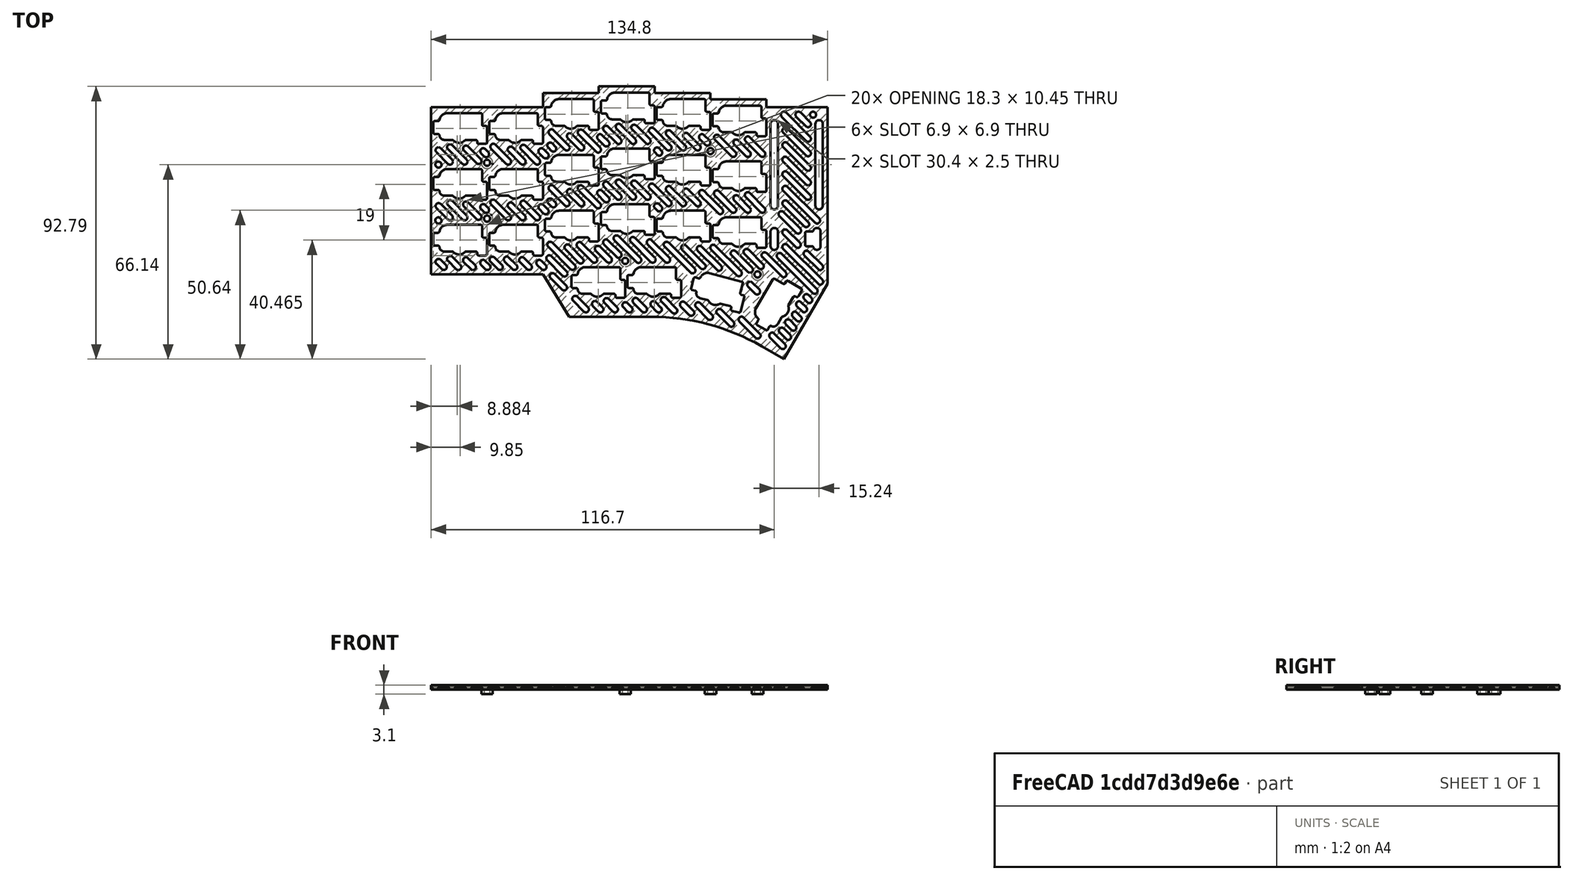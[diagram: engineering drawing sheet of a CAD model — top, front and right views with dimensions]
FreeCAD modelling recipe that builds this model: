
FCSTD DOCUMENT  (FreeCAD 0.22R37213 (Git))
Label: key-v3
License: All rights reserved
LicenseURL: https://en.wikipedia.org/wiki/All_rights_reserved
objects: Sketcher::SketchObject×8, PartDesign::Pocket×5, PartDesign::Pad×4, Part::Part2DObjectPython×3, PartDesign::Body×3, Part::Cut×3, App::Link×2, PartDesign::LinearPattern×2, Spreadsheet::Sheet×1, Part::FeaturePython×1, PartDesign::FeatureBase×1, PartDesign::Plane×1
note: 40 computed .brp shape members not serialized (recipe doc carries the construction recipe); baked Part::Feature solids carry a one-line shape summary decoded from their .brp

FEATURE [Sketcher::SketchObject] Sketch  label="smd cutout"
  FullyConstrained = true
  sketch-geometry (67):
    g0: LineSegment StartX=-9.5 StartY=-9.5 StartZ=0 EndX=9.5 EndY=-9.5 EndZ=0
    g1: LineSegment StartX=9.5 StartY=-9.5 StartZ=0 EndX=9.5 EndY=9.5 EndZ=0
    g2: LineSegment StartX=9.5 StartY=9.5 StartZ=0 EndX=-9.5 EndY=9.5 EndZ=0
    g3: LineSegment StartX=-9.5 StartY=9.5 StartZ=0 EndX=-9.5 EndY=-9.5 EndZ=0
    g4: Circle CenterX=-3.81 CenterY=2.54 CenterZ=0 NormalX=0 NormalY=0 NormalZ=1 AngleXU=0 Radius=1.5
    g5: Circle CenterX=2.54 CenterY=5.08 CenterZ=0 NormalX=0 NormalY=0 NormalZ=1 AngleXU=0 Radius=1.5
    g6: Circle CenterX=0 CenterY=0 CenterZ=0 NormalX=0 NormalY=0 NormalZ=1 AngleXU=0 Radius=2
    g7: Circle CenterX=5 CenterY=0 CenterZ=0 NormalX=0 NormalY=0 NormalZ=1 AngleXU=0 Radius=1
    g8: Circle CenterX=-5 CenterY=0 CenterZ=0 NormalX=0 NormalY=0 NormalZ=1 AngleXU=0 Radius=1
    g9: GeomPoint X=-8.5 Y=1 Z=0
    g10: GeomPoint X=-8.5 Y=4 Z=0
    g11: GeomPoint X=-6 Y=4 Z=0
    g12: GeomPoint X=-2.5 Y=1 Z=0
    g13: GeomPoint X=-0.4 Y=2.9 Z=0
    g14: GeomPoint X=4.5 Y=2.9 Z=0
    g15: GeomPoint X=4.5 Y=3.6 Z=0
    g16: GeomPoint X=7.1 Y=6.7 Z=0
    g17: GeomPoint X=-4 Y=6.7 Z=0
    g18: LineSegment StartX=-8.5 StartY=1 StartZ=0 EndX=-2.5 EndY=1 EndZ=0
    g19: LineSegment StartX=-8.5 StartY=1 StartZ=0 EndX=-8.5 EndY=4 EndZ=0
    g20: LineSegment StartX=-8.5 StartY=4 StartZ=0 EndX=-6 EndY=4 EndZ=0
    g21: LineSegment StartX=-6 StartY=4 StartZ=0 EndX=-6 EndY=4.7 EndZ=0
    g22: LineSegment StartX=-4 StartY=6.7 StartZ=0 EndX=7.1 EndY=6.7 EndZ=0
    g23: LineSegment StartX=7.1 StartY=6.7 StartZ=0 EndX=7.1 EndY=3.6 EndZ=0
    g24: LineSegment StartX=7.1 StartY=3.6 StartZ=0 EndX=4.5 EndY=3.6 EndZ=0
    g25: LineSegment StartX=4.5 StartY=2.9 StartZ=0 EndX=4.5 EndY=3.6 EndZ=0
    g26: LineSegment StartX=4.5 StartY=2.9 StartZ=0 EndX=-0.4 EndY=2.9 EndZ=0
    g27: ArcOfCircle CenterX=-0.4 CenterY=0.789474 CenterZ=0 NormalX=0 NormalY=0 NormalZ=1 AngleXU=0 Radius=2.11053 StartAngle=1.5708 EndAngle=3.04168
    g28: LineSegment StartX=6.85 StartY=2.35 StartZ=0 EndX=6.85 EndY=-2.35 EndZ=0
    g29: LineSegment StartX=6.85 StartY=-2.35 StartZ=0 EndX=9.15 EndY=-2.35 EndZ=0
    g30: LineSegment StartX=9.15 StartY=-2.35 StartZ=0 EndX=9.15 EndY=2.35 EndZ=0
    g31: ArcOfCircle CenterX=-4 CenterY=4.7 CenterZ=0 NormalX=0 NormalY=0 NormalZ=1 AngleXU=0 Radius=2 StartAngle=1.5708 EndAngle=3.14159
    g32: LineSegment StartX=6.85 StartY=2.35 StartZ=0 EndX=9.15 EndY=2.35 EndZ=0
    g33: LineSegment StartX=-8.8 StartY=0.8 StartZ=0 EndX=-8.8 EndY=4.2 EndZ=0
    g34: LineSegment StartX=-8.3 StartY=4.7 StartZ=0 EndX=-7.1607 EndY=4.7 EndZ=0
    g35: LineSegment StartX=-4 StartY=7.4 StartZ=0 EndX=7.3 EndY=7.4 EndZ=0
    g36: LineSegment StartX=7.8 StartY=6.9 StartZ=0 EndX=7.8 EndY=3.55 EndZ=0
    g37: LineSegment StartX=9.5 StartY=2.55 StartZ=0 EndX=9.5 EndY=-2.55 EndZ=0
    g38: LineSegment StartX=9 StartY=-3.05 StartZ=0 EndX=6.65 EndY=-3.05 EndZ=0
    g39: LineSegment StartX=-8.3 StartY=0.3 StartZ=0 EndX=-7.19089 EndY=0.3 EndZ=0
    g40: ArcOfCircle CenterX=-5 CenterY=0 CenterZ=0 NormalX=0 NormalY=0 NormalZ=1 AngleXU=0 Radius=1.7 StartAngle=3.23263 EndAngle=4.71239
    g41: ArcOfCircle CenterX=0 CenterY=0 CenterZ=0 NormalX=0 NormalY=0 NormalZ=1 AngleXU=0 Radius=2.7 StartAngle=3.89963 EndAngle=5.52514
    g42: LineSegment StartX=-5 StartY=-1.7 StartZ=0 EndX=-2.32379 EndY=-1.7 EndZ=0
    g43: LineSegment StartX=6.15 StartY=-2.55 StartZ=0 EndX=6.15 EndY=-2.2 EndZ=0
    g44: LineSegment StartX=2.32379 StartY=-1.7 StartZ=0 EndX=5.65 EndY=-1.7 EndZ=0
    g45: ArcOfCircle CenterX=-4 CenterY=4.7 CenterZ=0 NormalX=0 NormalY=0 NormalZ=1 AngleXU=0 Radius=2.7 StartAngle=1.5708 EndAngle=2.9847
    g46: ArcOfCircle CenterX=-2.32379 CenterY=-2.2 CenterZ=0 NormalX=0 NormalY=0 NormalZ=1 AngleXU=0 Radius=0.5 StartAngle=0.758041 EndAngle=1.5708
    g47: ArcOfCircle CenterX=2.32379 CenterY=-2.2 CenterZ=0 NormalX=0 NormalY=0 NormalZ=1 AngleXU=0 Radius=0.5 StartAngle=1.5708 EndAngle=2.38355
    g48: ArcOfCircle CenterX=5.65 CenterY=-2.2 CenterZ=0 NormalX=0 NormalY=0 NormalZ=1 AngleXU=0 Radius=0.5 StartAngle=0 EndAngle=1.5708
    g49: GeomPoint X=6.15 Y=-1.7 Z=0
    g50: ArcOfCircle CenterX=6.65 CenterY=-2.55 CenterZ=0 NormalX=0 NormalY=0 NormalZ=1 AngleXU=0 Radius=0.5 StartAngle=3.14159 EndAngle=4.71239
    g51: GeomPoint X=6.15 Y=-3.05 Z=0
    g52: ArcOfCircle CenterX=9 CenterY=-2.55 CenterZ=0 NormalX=0 NormalY=0 NormalZ=1 AngleXU=0 Radius=0.5 StartAngle=4.71239 EndAngle=6.28319
    g53: GeomPoint X=9.5 Y=-3.05 Z=0
    g54: LineSegment StartX=8.3 StartY=3.05 StartZ=0 EndX=9 EndY=3.05 EndZ=0
    g55: ArcOfCircle CenterX=9 CenterY=2.55 CenterZ=0 NormalX=0 NormalY=0 NormalZ=1 AngleXU=0 Radius=0.5 StartAngle=3e-16 EndAngle=1.5708
    g56: GeomPoint X=9.5 Y=3.05 Z=0
    g57: ArcOfCircle CenterX=8.3 CenterY=3.55 CenterZ=0 NormalX=0 NormalY=0 NormalZ=1 AngleXU=0 Radius=0.5 StartAngle=3.14159 EndAngle=4.71239
    g58: GeomPoint X=7.8 Y=3.05 Z=0
    g59: ArcOfCircle CenterX=7.3 CenterY=6.9 CenterZ=0 NormalX=0 NormalY=0 NormalZ=1 AngleXU=0 Radius=0.5 StartAngle=-9e-16 EndAngle=1.5708
    g60: GeomPoint X=7.8 Y=7.4 Z=0
    g61: ArcOfCircle CenterX=-7.1607 CenterY=5.2 CenterZ=0 NormalX=0 NormalY=0 NormalZ=1 AngleXU=0 Radius=0.5 StartAngle=4.71239 EndAngle=6.12629
    g62: ArcOfCircle CenterX=-8.3 CenterY=4.2 CenterZ=0 NormalX=0 NormalY=0 NormalZ=1 AngleXU=0 Radius=0.5 StartAngle=1.5708 EndAngle=3.14159
    g63: GeomPoint X=-8.8 Y=4.7 Z=0
    g64: ArcOfCircle CenterX=-8.3 CenterY=0.8 CenterZ=0 NormalX=0 NormalY=0 NormalZ=1 AngleXU=0 Radius=0.5 StartAngle=3.14159 EndAngle=4.71239
    g65: GeomPoint X=-8.8 Y=0.3 Z=0
    g66: ArcOfCircle CenterX=-7.19089 CenterY=-0.2 CenterZ=0 NormalX=0 NormalY=0 NormalZ=1 AngleXU=0 Radius=0.5 StartAngle=0.0910348 EndAngle=1.5708
  constraints (157):
    c: Coincident(g2,g3)
    c: Horizontal(g0)
    c: Horizontal(g2)
    c: Vertical(g1)
    c: PointOnObject(g7,g-1)
    c: Equal(g4,g5)
    c: Symmetric(g7,g8,g-2)
    c: Equal(g8,g7)
    c: DistanceX(g-1,g5) = 2.54
    c: Distance(g5,g-1) = 5.08
    c: DistanceX(g2,g2) = 19
    c: Equal(g2,g3)
    c: Distance(g4,g-2) = 3.81
    c: Distance(g4,g-1) = 2.54
    c: Distance(g8,g-2) = 5
    c: Distance(g9,g-1) = 1
    c: Coincident(g18,g9)
    c: Coincident(g18,g12)
    c: Horizontal(g18)
    c: Distance(g9,g-2) = 8.5
    c: Coincident(g19,g9)
    c: Coincident(g19,g10)
    c: Vertical(g19)
    c: Distance(g10,g-1) = 4
    c: Coincident(g20,g10)
    c: Coincident(g20,g11)
    c: Horizontal(g20)
    c: Distance(g11,g-2) = 6
    c: Distance(g17,g-2) = 4
    c: DistanceY(g-1,g17) = 6.7
    c: Coincident(g21,g11)
    c: Vertical(g21)
    c: Coincident(g22,g17)
    c: Coincident(g22,g16)
    c: Horizontal(g22)
    c: DistanceX(g-1,g16) = 7.1
    c: Coincident(g23,g16)
    c: Vertical(g23)
    c: Distance(g23,g-1) = 3.6
    c: Coincident(g24,g23)
    c: Coincident(g24,g15)
    c: Coincident(g25,g14)
    c: Coincident(g25,g15)
    c: Coincident(g26,g14)
    c: Coincident(g26,g13)
    c: Horizontal(g24)
    c: Horizontal(g26)
    c: Vertical(g25)
    c: Distance(g-2,g25) = 4.5
    c: Distance(g14,g-1) = 2.9
    c: Distance(g13,g-2) = 0.4
    c: Distance(g12,g-2) = 2.5
    c: Coincident(g27,g13)
    c: Coincident(g27,g12)
    c: Diameter(g5) = 3
    c: Diameter(g8) = 2
    c: Diameter(g6) = 4
    c: Vertical(g30)
    c: Horizontal(g29)
    c: Distance(g28,g-2) = 6.85
    c: Distance(g28,g-1) = 2.35
    c: Symmetric(g28,g28,g-1)
    c: Vertical(g3)
    c: Coincident(g31,g17)
    c: Tangent(g31,g21) = 1.5708
    c: Coincident(g32,g28)
    c: Coincident(g32,g30)
    c: Horizontal(g32)
    c: Coincident(g6,g-1)
    c: Symmetric(g0,g1,g6)
    c: Coincident(g3,g0)
    c: Coincident(g2,g1)
    c: Coincident(g1,g0)
    c: DistanceX(g29,g29) = 2.3
    c: Coincident(g29,g30)
    c: Coincident(g29,g28)
    c: Tangent(g27,g26)
    c: Tangent(g31,g22)
    c: Vertical(g33)
    c: Horizontal(g34)
    c: Horizontal(g35)
    c: Vertical(g36)
    c: PointOnObject(g56,g1)
    c: PointOnObject(g53,g1)
    c: Horizontal(g38)
    c: Horizontal(g39)
    c: Distance(g20,g34) = 0.7
    c: Distance(g65,g19) = 0.3
    c: Distance(g18,g39) = 0.7
    c: Coincident(g40,g8)
    c: Coincident(g41,g6)
    c: Horizontal(g42)
    c: Vertical(g43)
    c: Tangent(g44,g42)
    c: Distance(g28,g43) = 0.7
    c: Distance(g53,g29) = 0.7
    c: Tangent(g42,g40) = -1.5708
    c: Distance(g23,g36) = 0.7
    c: Distance(g35,g22) = 0.7
    c: Coincident(g45,g31)
    c: Tangent(g45,g35) = 1.5708
    c: Tangent(g42,g46) = 1.5708
    c: Tangent(g41,g46) = 1.5708
    c: Tangent(g41,g47) = 1.5708
    c: Tangent(g44,g47) = 1.5708
    c: PointOnObject(g49,g44)
    c: PointOnObject(g49,g43)
    c: Tangent(g44,g48) = 1.5708
    c: Tangent(g43,g48) = -1.5708
    c: PointOnObject(g51,g43)
    c: PointOnObject(g51,g38)
    c: Tangent(g43,g50) = 1.5708
    c: Tangent(g38,g50) = 1.5708
    c: PointOnObject(g53,g38)
    c: PointOnObject(g53,g37)
    c: Tangent(g38,g52) = 1.5708
    c: Tangent(g37,g52) = 1.5708
    c: Horizontal(g54)
    c: Distance(g32,g54) = 0.7
    c: PointOnObject(g56,g37)
    c: PointOnObject(g56,g54)
    c: Tangent(g37,g55) = 1.5708
    c: Tangent(g54,g55) = 1.5708
    c: PointOnObject(g58,g54)
    c: PointOnObject(g58,g36)
    c: Tangent(g54,g57) = -1.5708
    c: Tangent(g36,g57) = -1.5708
    c: PointOnObject(g60,g35)
    c: PointOnObject(g60,g36)
    c: Tangent(g35,g59) = 1.5708
    c: Tangent(g36,g59) = 1.5708
    c: Tangent(g34,g61) = -1.5708
    c: Tangent(g45,g61) = 1.5708
    c: PointOnObject(g63,g34)
    c: PointOnObject(g63,g33)
    c: Tangent(g34,g62) = 1.5708
    c: Tangent(g33,g62) = 1.5708
    c: PointOnObject(g65,g39)
    c: PointOnObject(g65,g33)
    c: Tangent(g39,g64) = -1.5708
    c: Tangent(g33,g64) = 1.5708
    c: Tangent(g40,g66) = 1.5708
    c: Tangent(g39,g66) = 1.5708
    c: Radius(g46) = 0.5
    c: Equal(g66,g64)
    c: Equal(g64,g46)
    c: Equal(g46,g47)
    c: Equal(g47,g48)
    c: Equal(g48,g50)
    c: Equal(g50,g57)
    c: Equal(g57,g59)
    c: Equal(g59,g61)
    c: Equal(g61,g62)
    c: Equal(g57,g55)
    c: Equal(g52,g50)
    c: Distance(g40,g8) = 0.7
    c: Distance(g41,g6) = 0.7
FEATURE [Spreadsheet::Sheet] Spreadsheet  label="constants"
  cells = A1(slot_height)=0.6; B1='slot height; A2(base_normal)=1.5; B2='base normal; A3(base_thin)=0.3; B3='base thin ; A4(fillet_small)=0.15; B4='fillet rounding
FEATURE [Part::Part2DObjectPython] Wire  # Draft 2D object (typed FeaturePython)
  Area = 0
  ChamferSize = 0
  Closed = false
  End = (95,2.6,0)
  FilletRadius = 0
  Length = 95.9778
  MakeFace = true
  Points = (6) [(0,0,0),(19,0,0),(38,4.8,0),(57,7,0),(76,4.8,0),(95,2.6,0)]
  Start = (0,0,0)
  Subdivisions = 0
FEATURE [Part::Part2DObjectPython] Wire001  label="main matrix wire"  # Draft 2D object (typed FeaturePython)
  Area = 0
  ChamferSize = 0
  Closed = false
  End = (95,2.6,0)
  FilletRadius = 0
  Length = 323.978
  MakeFace = false
  Points = (18) [(0,0,0),(0,-19,0),(0,-38,0),(19,-38,0),(19,-19,0),(19,0,0),(38,4.8,0),(38,-14.2,0),(38,-33.2,0),(57,-31,0),(57,-12,0),(57,7,0),(76,4.8,0),+5 more]
  Start = (0,0,0)
  Subdivisions = 0
FEATURE [Part::Part2DObjectPython] Wire002  label="horizonal matrix"  # Draft 2D object (typed FeaturePython)
  Area = 0
  ChamferSize = 0
  Closed = false
  End = (95,2.6,0)
  FilletRadius = 0
  Length = 368.271
  MakeFace = true
  Points = (20) [(0,0,0),(0,-19,0),(0,-38,0),(19,-38,0),(19,-19,0),(19,0,0),(38,4.8,0),(38,-14.2,0),(38,-33.2,0),(47,-52.4,0),(66,-52.4,0),(57,-31,0),(57,-12,0),+7 more]
  Start = (0,0,0)
  Subdivisions = 0
FEATURE [Sketcher::SketchObject] Sketch001  label="pcb contour"
  AttachmentSupport = -> [XY_Plane]
  FullyConstrained = true
  MapMode = 5
  expr: Constraints[36] = 19 * 3
  sketch-geometry (39):
    g0: LineSegment StartX=-9.5 StartY=9.5 StartZ=0 EndX=28.5 EndY=9.5 EndZ=0
    g1: LineSegment StartX=28.5 StartY=9.5 StartZ=0 EndX=28.5 EndY=14.3 EndZ=0
    g2: LineSegment StartX=28.5 StartY=14.3 StartZ=0 EndX=47.5 EndY=14.3 EndZ=0
    g3: LineSegment StartX=47.5 StartY=14.3 StartZ=0 EndX=47.5 EndY=16.5 EndZ=0
    g4: LineSegment StartX=47.5 StartY=16.5 StartZ=0 EndX=66.5 EndY=16.5 EndZ=0
    g5: LineSegment StartX=66.5 StartY=16.5 StartZ=0 EndX=66.5 EndY=14.3 EndZ=0
    g6: LineSegment StartX=66.5 StartY=14.3 StartZ=0 EndX=85.5 EndY=14.3 EndZ=0
    g7: LineSegment StartX=85.5 StartY=14.3 StartZ=0 EndX=85.5 EndY=12.1 EndZ=0
    g8: LineSegment StartX=85.5 StartY=12.1 StartZ=0 EndX=104.5 EndY=12.1 EndZ=0
    g9: LineSegment StartX=104.5 StartY=12.1 StartZ=0 EndX=104.5 EndY=9.4 EndZ=0
    g10: LineSegment StartX=104.5 StartY=9.4 StartZ=0 EndX=125.3 EndY=9.4 EndZ=0
    g11: LineSegment StartX=-9.5 StartY=9.5 StartZ=0 EndX=-9.5 EndY=-47.5 EndZ=0
    g12: LineSegment StartX=-9.5 StartY=-47.5 StartZ=0 EndX=28.5 EndY=-47.5 EndZ=0
    g13: LineSegment StartX=28.5 StartY=-47.5 StartZ=0 EndX=37.45 EndY=-61.9 EndZ=0
    g14: LineSegment StartX=37.45 StartY=-61.9 StartZ=0 EndX=56.45 EndY=-61.9 EndZ=0
    g15: LineSegment StartX=56.45 StartY=-61.9 StartZ=0 EndX=56.45 EndY=-42.9 EndZ=0
    g16: LineSegment StartX=56.45 StartY=-42.9 StartZ=0 EndX=37.45 EndY=-42.9 EndZ=0
    g17: LineSegment StartX=37.45 StartY=-42.9 StartZ=0 EndX=37.45 EndY=-61.9 EndZ=0
    g18: LineSegment StartX=56.45 StartY=-61.9 StartZ=0 EndX=75.45 EndY=-61.9 EndZ=0
    g19: LineSegment StartX=75.45 StartY=-61.9 StartZ=0 EndX=75.45 EndY=-42.9 EndZ=0
    g20: LineSegment StartX=75.45 StartY=-42.9 StartZ=0 EndX=56.45 EndY=-42.9 EndZ=0
    g21: LineSegment StartX=56.45 StartY=-42.9 StartZ=0 EndX=56.45 EndY=-61.9 EndZ=0
    g22: GeomPoint X=65.95 Y=-52.4 Z=0
    g23: LineSegment StartX=110.452 StartY=-76.2909 StartZ=0 EndX=93.9978 EndY=-66.7909 EndZ=0
    g24: LineSegment StartX=93.9978 StartY=-66.7909 StartZ=0 EndX=108.248 EndY=-42.1091 EndZ=0
    g25: LineSegment StartX=108.248 StartY=-42.1091 StartZ=0 EndX=124.702 EndY=-51.6091 EndZ=0
    g26: LineSegment StartX=124.702 StartY=-51.6091 StartZ=0 EndX=110.452 EndY=-76.2909 EndZ=0
    g27: GeomPoint X=109.35 Y=-59.2 Z=0
    g28: LineSegment StartX=75.5149 StartY=-61.9175 StartZ=0 EndX=80.4325 EndY=-43.5649 EndZ=0
    g29: LineSegment StartX=80.4325 StartY=-43.5649 StartZ=0 EndX=98.7851 EndY=-48.4825 EndZ=0
    g30: LineSegment StartX=98.7851 StartY=-48.4825 StartZ=0 EndX=93.8675 EndY=-66.8351 EndZ=0
    g31: LineSegment StartX=93.8675 StartY=-66.8351 StartZ=0 EndX=75.5149 EndY=-61.9175 EndZ=0
    g32: GeomPoint X=87.15 Y=-55.2 Z=0
    g33: LineSegment StartX=37.45 StartY=-61.9 StartZ=0 EndX=65.4303 EndY=-61.9 EndZ=0
    g34: LineSegment StartX=110.452 StartY=-76.2909 StartZ=0 EndX=102.93 EndY=-71.9481 EndZ=0
    g35: LineSegment StartX=125.3 StartY=9.4 StartZ=0 EndX=125.3 EndY=-50.5738 EndZ=0
    g36: LineSegment StartX=110.452 StartY=-76.2909 StartZ=0 EndX=125.3 EndY=-50.5738 EndZ=0
    g37: ArcOfCircle CenterX=65.4303 CenterY=-136.9 CenterZ=0 NormalX=0 NormalY=0 NormalZ=1 AngleXU=0 Radius=75 StartAngle=1.0472 EndAngle=1.5708
    g38: GeomPoint X=85.5265 Y=-61.9 Z=0
  constraints (105):
    c: Horizontal(g0)
    c: Coincident(g1,g0)
    c: Vertical(g1)
    c: Coincident(g2,g1)
    c: Horizontal(g2)
    c: Coincident(g3,g2)
    c: Vertical(g3)
    c: Coincident(g4,g3)
    c: Horizontal(g4)
    c: Coincident(g5,g4)
    c: Vertical(g5)
    c: Coincident(g6,g5)
    c: Horizontal(g6)
    c: Coincident(g7,g6)
    c: Vertical(g7)
    c: Coincident(g8,g7)
    c: Horizontal(g8)
    c: Coincident(g9,g8)
    c: Vertical(g9)
    c: Coincident(g10,g9)
    c: Horizontal(g10)
    c: DistanceX(g0,g-1) = 9.5
    c: Distance(g-1,g0) = 9.5
    c: DistanceX(g0,g0) = 38
    c: DistanceX(g2,g2) = 19
    c: Equal(g4,g2)
    c: Equal(g2,g6)
    c: Equal(g6,g8)
    c: DistanceY(g1,g1) = 4.8
    c: DistanceY(g3,g3) = 2.2
    c: DistanceY(g5,g5) = 2.2
    c: DistanceY(g7,g7) = 2.2
    c: DistanceY(g9,g9) = 2.7
    c: DistanceX(g10,g10) = 20.8
    c: Coincident(g11,g0)
    c: Vertical(g11)
    c: DistanceY(g11,g11) = 57
    c: Coincident(g12,g11)
    c: Horizontal(g12)
    c: DistanceX(g12,g12) = 38
    c: Coincident(g13,g12)
    c: DistanceX(g12,g13) = 8.95
    c: DistanceY(g13,g12) = 14.4
    c: Coincident(g14,g15)
    c: Coincident(g15,g16)
    c: Coincident(g16,g17)
    c: Coincident(g17,g14)
    c: Horizontal(g14)
    c: Horizontal(g16)
    c: Vertical(g15)
    c: Vertical(g17)
    c: Coincident(g14,g13)
    c: Equal(g17,g16)
    c: DistanceX(g16,g16) = 19
    c: Coincident(g18,g19)
    c: Coincident(g19,g20)
    c: Coincident(g20,g21)
    c: Coincident(g21,g18)
    c: Horizontal(g18)
    c: Horizontal(g20)
    c: Vertical(g19)
    c: Vertical(g21)
    c: Coincident(g18,g14)
    c: Equal(g20,g19)
    c: Equal(g19,g16)
    c: Symmetric(g14,g19,g22)
    c: Coincident(g24,g23)
    c: Coincident(g25,g24)
    c: Coincident(g26,g25)
    c: Coincident(g26,g23)
    c: Parallel(g25,g23)
    c: Parallel(g24,g26)
    c: Perpendicular(g25,g24)
    c: Equal(g23,g19)
    c: Symmetric(g25,g23,g27)
    c: Coincident(g29,g28)
    c: Coincident(g30,g29)
    c: Coincident(g31,g30)
    c: Coincident(g31,g28)
    c: Parallel(g30,g28)
    c: Parallel(g29,g31)
    c: Perpendicular(g30,g29)
    c: Equal(g29,g28)
    c: Symmetric(g30,g28,g32)
    c: Angle(g31,g18) = 0.261799
    c: Angle(g18,g26) = 1.0472
    c: DistanceX(g22,g32) = 21.2
    c: DistanceY(g32,g22) = 2.8
    c: Equal(g28,g19)
    c: DistanceX(g32,g27) = 22.2
    c: DistanceY(g27,g32) = 4
    c: Distance(g26,g26) = 28.5
    c: Coincident(g33,g13)
    c: Horizontal(g33)
    c: Tangent(g34,g23) = -1.5708
    c: Coincident(g35,g10)
    c: Vertical(g35)
    c: Coincident(g36,g23)
    c: Tangent(g26,g36)
    c: Coincident(g36,g35)
    c: PointOnObject(g38,g34)
    c: PointOnObject(g38,g33)
    c: Tangent(g34,g37) = -1.5708
    c: Tangent(g33,g37) = 1.5708
    c: Radius(g37) = 75
FEATURE [PartDesign::Pad] Pad  label="base"
  Direction = (0,0,1)
  Length = 1.5
  Length2 = 10
  Profile = -> Sketch001
  ReferenceAxis = -> Sketch001 [N_Axis]
  Suppressed = false
  Type = 0
  expr: Length = <<constants>>.base_normal
FEATURE [PartDesign::Body] Body  label="base body"
  Group = -> [Sketch001,Pad]
  Origin = -> Origin
  Tip = -> Pad
FEATURE [PartDesign::Pad] Pad001
  Direction = (0,0,1)
  Length = 1.5
  Length2 = 10
  Profile = -> Sketch
  ReferenceAxis = -> Sketch [N_Axis]
  Suppressed = false
  Type = 0
  expr: Length = <<constants>>.base_normal
FEATURE [PartDesign::Body] Body001  label="cutout"
  Group = -> [Sketch,Pad001]
  Origin = -> Origin001
  Tip = -> Pad001
FEATURE [Part::FeaturePython] PointArray  label="cutout array"  # Draft array (typed FeaturePython)
  Base = -> Body001
  Count = 20
  Fuse = false
  PointObject = -> Wire002
FEATURE [App::Link] Link  label="cutout001"
  LinkPlacement = pos=(87.2,-55.2,0) rot=(0,0,1;6.02139rad)
  LinkedObject = -> Body001
  Placement = pos=(87.2,-55.2,0) rot=(0,0,1;6.02139rad)
FEATURE [App::Link] Link001  label="cutout002"
  LinkPlacement = pos=(109.4,-59.2,0) rot=(0,0,1;1.0472rad)
  LinkedObject = -> Body001
  Placement = pos=(109.4,-59.2,0) rot=(0,0,1;1.0472rad)
FEATURE [Part::Cut] Cut
  Base = -> Body
  Tool = -> PointArray
FEATURE [Part::Cut] Cut001
  Base = -> Cut
  Tool = -> Link
FEATURE [Part::Cut] Cut002
  Base = -> Cut001
  Tool = -> Link001
FEATURE [PartDesign::FeatureBase] BaseFeature
  BaseFeature = -> Cut002
  Suppressed = false
FEATURE [PartDesign::Plane] DatumPlane
  AttachmentSupport = -> [BaseFeature,Z_Axis003]
  Length = 196.764
  MapMode = 13
  Placement = pos=(-6.33333,6.33333,0.5) rot=(0.281085,0.678598,0.678598;2.59356rad)
  ResizeMode = 0
  Width = 68.8627
FEATURE [Sketcher::SketchObject] Sketch003
  AttachmentSupport = -> [DatumPlane]
  ExternalGeometry = -> [BaseFeature]
  FullyConstrained = true
  MapMode = 5
  Placement = pos=(-6.33333,6.33333,0.5) rot=(0.281085,0.678598,0.678598;2.59356rad)
  expr: Constraints[6] = <<constants>>.slot_height
  expr: Constraints[9] = <<constants>>.base_thin
  sketch-geometry (4):
    g0: ArcOfCircle CenterX=2.17834 CenterY=0.1 CenterZ=0 NormalX=0 NormalY=0 NormalZ=1 AngleXU=0 Radius=0.3 StartAngle=4.71239 EndAngle=7.85398
    g1: ArcOfCircle CenterX=0.178343 CenterY=0.1 CenterZ=0 NormalX=0 NormalY=0 NormalZ=1 AngleXU=0 Radius=0.3 StartAngle=1.5708 EndAngle=4.71239
    g2: LineSegment StartX=2.17834 StartY=-0.2 StartZ=0 EndX=0.178343 EndY=-0.2 EndZ=0
    g3: LineSegment StartX=2.17834 StartY=0.4 StartZ=0 EndX=0.178343 EndY=0.4 EndZ=0
  constraints (10):
    c: Tangent(g0,g2) = 1.5708
    c: Tangent(g0,g3) = -1.5708
    c: Tangent(g1,g2) = 1.5708
    c: Tangent(g1,g3) = -1.5708
    c: Equal(g0,g1)
    c: Horizontal(g2)
    c: Distance(g3,g2) = 0.6
    c: DistanceX(g1,g0) = 2
    c: Distance(g0,g-4) = 2
    c: Distance(g-5,g2) = 0.3
FEATURE [PartDesign::Pocket] Pocket
  BaseFeature = -> BaseFeature
  Direction = (-0.707107,-0.707107,0)
  Length = 5
  Length2 = 5
  Midplane = true
  Profile = -> Sketch003
  ReferenceAxis = -> Sketch003 [N_Axis]
  Suppressed = false
  Type = 1
FEATURE [PartDesign::LinearPattern] LinearPattern
  BaseFeature = -> Pocket
  Direction = -> Sketch003 [H_Axis]
  Length = 156
  Mode = 1
  Occurrences = 40
  Offset = 4
  Originals = -> [Pocket]
  Reversed = true
  Suppressed = false
FEATURE [Sketcher::SketchObject] Sketch004
  AttachmentSupport = -> [LinearPattern]
  FullyConstrained = true
  MapMode = 5
  Placement = pos=(0,0,0) rot=(1,0,0;3.14159rad)
  expr: Constraints[5] = 9.5 + 19
  sketch-geometry (5):
    g0: Circle CenterX=9.5 CenterY=9.5 CenterZ=0 NormalX=0 NormalY=0 NormalZ=1 AngleXU=0 Radius=1.95
    g1: Circle CenterX=9.5 CenterY=28.5 CenterZ=0 NormalX=0 NormalY=0 NormalZ=1 AngleXU=0 Radius=1.95
    g2: Circle CenterX=56.5 CenterY=42.9 CenterZ=0 NormalX=0 NormalY=0 NormalZ=1 AngleXU=0 Radius=1.95
    g3: Circle CenterX=85.5 CenterY=5.5 CenterZ=0 NormalX=0 NormalY=0 NormalZ=1 AngleXU=0 Radius=1.95
    g4: Circle CenterX=101.5 CenterY=47.5 CenterZ=0 NormalX=0 NormalY=0 NormalZ=1 AngleXU=0 Radius=1.95
  constraints (15):
    c: Diameter(g0) = 3.9
    c: DistanceY(g-1,g0) = 9.5
    c: DistanceX(g-1,g0) = 9.5
    c: Equal(g1,g0)
    c: Distance(g1,g-2) = 9.5
    c: Distance(g1,g-1) = 28.5
    c: DistanceX(g-1,g2) = 56.5
    c: DistanceY(g-1,g2) = 42.9
    c: Equal(g2,g3)
    c: Equal(g3,g1)
    c: DistanceX(g-1,g3) = 85.5
    c: DistanceY(g-1,g3) = 5.5
    c: DistanceX(g-1,g4) = 101.5
    c: DistanceY(g-1,g4) = 47.5
    c: Equal(g4,g0)
FEATURE [PartDesign::Pad] Pad002
  BaseFeature = -> LinearPattern
  Direction = (0,0,-1)
  Length = 1.6
  Length2 = 10
  Profile = -> Sketch004
  ReferenceAxis = -> Sketch004 [N_Axis]
  Suppressed = false
  Type = 0
FEATURE [Sketcher::SketchObject] Sketch005
  AttachmentSupport = -> [Pad002]
  ExternalGeometry = -> [Pad002]
  FullyConstrained = true
  MapMode = 5
  Placement = pos=(0,0,0) rot=(1,0,0;3.14159rad)
  sketch-geometry (100):
    g0: ArcOfCircle CenterX=-7 CenterY=5.21569 CenterZ=0 NormalX=0 NormalY=0 NormalZ=1 AngleXU=0 Radius=1 StartAngle=2.35619 EndAngle=5.49779
    g1: ArcOfCircle CenterX=-3.11569 CenterY=9.1 CenterZ=0 NormalX=0 NormalY=0 NormalZ=1 AngleXU=0 Radius=1 StartAngle=5.49779 EndAngle=8.63938
    g2: LineSegment StartX=-7.70711 StartY=5.9228 StartZ=0 EndX=-3.8228 EndY=9.80711 EndZ=0
    g3: LineSegment StartX=-6.29289 StartY=4.50858 StartZ=0 EndX=-2.40858 EndY=8.39289 EndZ=0
    g4: ArcOfCircle CenterX=-3.06594 CenterY=4.2 CenterZ=0 NormalX=0 NormalY=0 NormalZ=1 AngleXU=0 Radius=1 StartAngle=2.35619 EndAngle=5.49779
    g5: ArcOfCircle CenterX=1.83406 CenterY=9.1 CenterZ=0 NormalX=0 NormalY=0 NormalZ=1 AngleXU=0 Radius=1 StartAngle=5.49779 EndAngle=8.63938
    g6: LineSegment StartX=-3.77305 StartY=4.90711 StartZ=0 EndX=1.12695 EndY=9.80711 EndZ=0
    g7: LineSegment StartX=-2.35884 StartY=3.49289 StartZ=0 EndX=2.54117 EndY=8.39289 EndZ=0
    g8: ArcOfCircle CenterX=2.33172 CenterY=4.64791 CenterZ=0 NormalX=0 NormalY=0 NormalZ=1 AngleXU=0 Radius=1 StartAngle=2.35619 EndAngle=5.49779
    g9: ArcOfCircle CenterX=6.60687 CenterY=8.92306 CenterZ=0 NormalX=0 NormalY=0 NormalZ=1 AngleXU=0 Radius=1 StartAngle=5.49779 EndAngle=8.63938
    g10: LineSegment StartX=1.62461 StartY=5.35502 StartZ=0 EndX=5.89976 EndY=9.63016 EndZ=0
    g11: LineSegment StartX=3.03883 StartY=3.94081 StartZ=0 EndX=7.31397 EndY=8.21595 EndZ=0
    g12: ArcOfCircle CenterX=8.18356 CenterY=5.55 CenterZ=0 NormalX=0 NormalY=0 NormalZ=1 AngleXU=0 Radius=1 StartAngle=2.35619 EndAngle=5.49779
    g13: ArcOfCircle CenterX=9.19886 CenterY=6.56531 CenterZ=0 NormalX=0 NormalY=0 NormalZ=1 AngleXU=0 Radius=1 StartAngle=5.49779 EndAngle=8.63938
    g14: LineSegment StartX=7.47645 StartY=6.25711 StartZ=0 EndX=8.49176 EndY=7.27242 EndZ=0
    g15: LineSegment StartX=8.89066 StartY=4.84289 StartZ=0 EndX=9.90597 EndY=5.8582 EndZ=0
    g16: ArcOfCircle CenterX=11.6109 CenterY=4.02759 CenterZ=0 NormalX=0 NormalY=0 NormalZ=1 AngleXU=0 Radius=1 StartAngle=2.35619 EndAngle=5.49779
    g17: ArcOfCircle CenterX=16.6833 CenterY=9.1 CenterZ=0 NormalX=0 NormalY=0 NormalZ=1 AngleXU=0 Radius=1 StartAngle=5.49779 EndAngle=8.63938
    g18: LineSegment StartX=10.9038 StartY=4.73469 StartZ=0 EndX=15.9762 EndY=9.80711 EndZ=0
    g19: LineSegment StartX=12.318 StartY=3.32048 StartZ=0 EndX=17.3904 EndY=8.39289 EndZ=0
    g20: ArcOfCircle CenterX=17.5171 CenterY=4.98409 CenterZ=0 NormalX=0 NormalY=0 NormalZ=1 AngleXU=0 Radius=1 StartAngle=2.35619 EndAngle=5.49779
    g21: ArcOfCircle CenterX=21.6331 CenterY=9.1 CenterZ=0 NormalX=0 NormalY=0 NormalZ=1 AngleXU=0 Radius=1 StartAngle=5.49779 EndAngle=8.63938
    g22: LineSegment StartX=16.81 StartY=5.69119 StartZ=0 EndX=20.9259 EndY=9.80711 EndZ=0
    g23: LineSegment StartX=18.2242 StartY=4.27698 StartZ=0 EndX=22.3402 EndY=8.39289 EndZ=0
    g24: ArcOfCircle CenterX=21.8392 CenterY=4.35645 CenterZ=0 NormalX=0 NormalY=0 NormalZ=1 AngleXU=0 Radius=1 StartAngle=2.35619 EndAngle=5.49779
    g25: ArcOfCircle CenterX=26.5828 CenterY=9.1 CenterZ=0 NormalX=0 NormalY=0 NormalZ=1 AngleXU=0 Radius=1 StartAngle=5.49779 EndAngle=8.63938
    g26: LineSegment StartX=21.1321 StartY=5.06356 StartZ=0 EndX=25.8757 EndY=9.80711 EndZ=0
    g27: LineSegment StartX=22.5464 StartY=3.64934 StartZ=0 EndX=27.2899 EndY=8.39289 EndZ=0
    g28: ArcOfCircle CenterX=27.9825 CenterY=5.55 CenterZ=0 NormalX=0 NormalY=0 NormalZ=1 AngleXU=0 Radius=1 StartAngle=2.35619 EndAngle=5.49779
    g29: ArcOfCircle CenterX=29.4376 CenterY=7.00507 CenterZ=0 NormalX=0 NormalY=0 NormalZ=1 AngleXU=0 Radius=1 StartAngle=5.49779 EndAngle=8.63938
    g30: LineSegment StartX=27.2754 StartY=6.25711 StartZ=0 EndX=28.7305 EndY=7.71218 EndZ=0
    g31: LineSegment StartX=28.6897 StartY=4.84289 StartZ=0 EndX=30.1447 EndY=6.29796 EndZ=0
    g32: ArcOfCircle CenterX=31 CenterY=3.6177 CenterZ=0 NormalX=0 NormalY=0 NormalZ=1 AngleXU=0 Radius=1 StartAngle=2.35619 EndAngle=5.49779
    g33: ArcOfCircle CenterX=32.0584 CenterY=4.67609 CenterZ=0 NormalX=0 NormalY=0 NormalZ=1 AngleXU=0 Radius=1 StartAngle=5.49779 EndAngle=8.63938
    g34: LineSegment StartX=30.2929 StartY=4.32481 StartZ=0 EndX=31.3513 EndY=5.38319 EndZ=0
    g35: LineSegment StartX=31.7071 StartY=2.9106 StartZ=0 EndX=32.7655 EndY=3.96898 EndZ=0
    g36: ArcOfCircle CenterX=31.4259 CenterY=-0.906125 CenterZ=0 NormalX=0 NormalY=0 NormalZ=1 AngleXU=0 Radius=1 StartAngle=2.35619 EndAngle=5.49779
    g37: ArcOfCircle CenterX=36.632 CenterY=4.3 CenterZ=0 NormalX=0 NormalY=0 NormalZ=1 AngleXU=0 Radius=1 StartAngle=5.49779 EndAngle=8.63938
    g38: LineSegment StartX=30.7188 StartY=-0.199018 StartZ=0 EndX=35.9249 EndY=5.00711 EndZ=0
    g39: LineSegment StartX=32.133 StartY=-1.61323 StartZ=0 EndX=37.3392 EndY=3.59289 EndZ=0
    g40: ArcOfCircle CenterX=37.6714 CenterY=0.389607 CenterZ=0 NormalX=0 NormalY=0 NormalZ=1 AngleXU=0 Radius=1 StartAngle=2.35619 EndAngle=5.49779
    g41: ArcOfCircle CenterX=41.5818 CenterY=4.3 CenterZ=0 NormalX=0 NormalY=0 NormalZ=1 AngleXU=0 Radius=1 StartAngle=5.49779 EndAngle=8.63938
    g42: LineSegment StartX=36.9643 StartY=1.09671 StartZ=0 EndX=40.8747 EndY=5.00711 EndZ=0
    g43: LineSegment StartX=38.3785 StartY=-0.3175 StartZ=0 EndX=42.2889 EndY=3.59289 EndZ=0
    g44: ArcOfCircle CenterX=41.3817 CenterY=-0.849816 CenterZ=0 NormalX=0 NormalY=0 NormalZ=1 AngleXU=0 Radius=1 StartAngle=2.35619 EndAngle=5.49779
    g45: ArcOfCircle CenterX=47.2624 CenterY=5.03088 CenterZ=0 NormalX=0 NormalY=0 NormalZ=1 AngleXU=0 Radius=1 StartAngle=5.49779 EndAngle=8.63938
    g46: LineSegment StartX=40.6746 StartY=-0.142709 StartZ=0 EndX=46.5553 EndY=5.73799 EndZ=0
    g47: LineSegment StartX=42.0888 StartY=-1.55692 StartZ=0 EndX=47.9695 EndY=4.32378 EndZ=0
    g48: ArcOfCircle CenterX=47.9313 CenterY=0.75 CenterZ=0 NormalX=0 NormalY=0 NormalZ=1 AngleXU=0 Radius=1 StartAngle=2.35619 EndAngle=5.49779
    g49: ArcOfCircle CenterX=50.1391 CenterY=2.95777 CenterZ=0 NormalX=0 NormalY=0 NormalZ=1 AngleXU=0 Radius=1 StartAngle=5.49779 EndAngle=8.63938
    g50: LineSegment StartX=47.2242 StartY=1.45711 StartZ=0 EndX=49.4319 EndY=3.66487 EndZ=0
    g51: LineSegment StartX=48.6384 StartY=0.0428931 StartZ=0 EndX=50.8462 EndY=2.25066 EndZ=0
    g52: ArcOfCircle CenterX=50 CenterY=-2.13104 CenterZ=0 NormalX=0 NormalY=0 NormalZ=1 AngleXU=0 Radius=1 StartAngle=2.35619 EndAngle=5.49779
    g53: ArcOfCircle CenterX=54.231 CenterY=2.1 CenterZ=0 NormalX=0 NormalY=0 NormalZ=1 AngleXU=0 Radius=1 StartAngle=5.49779 EndAngle=8.63938
    g54: LineSegment StartX=49.2929 StartY=-1.42393 StartZ=0 EndX=53.5239 EndY=2.80711 EndZ=0
    g55: LineSegment StartX=50.7071 StartY=-2.83814 StartZ=0 EndX=54.9381 EndY=1.39289 EndZ=0
    g56: ArcOfCircle CenterX=54.2808 CenterY=-2.8 CenterZ=0 NormalX=0 NormalY=0 NormalZ=1 AngleXU=0 Radius=1 StartAngle=2.35619 EndAngle=5.49779
    g57: ArcOfCircle CenterX=59.1808 CenterY=2.1 CenterZ=0 NormalX=0 NormalY=0 NormalZ=1 AngleXU=0 Radius=1 StartAngle=5.49779 EndAngle=8.63938
    g58: LineSegment StartX=53.5737 StartY=-2.09289 StartZ=0 EndX=58.4737 EndY=2.80711 EndZ=0
    g59: LineSegment StartX=54.9879 StartY=-3.50711 StartZ=0 EndX=59.8879 EndY=1.39289 EndZ=0
    g60: ArcOfCircle CenterX=59.5579 CenterY=-2.47263 CenterZ=0 NormalX=0 NormalY=0 NormalZ=1 AngleXU=0 Radius=1 StartAngle=2.35619 EndAngle=5.49779
    g61: ArcOfCircle CenterX=64.1305 CenterY=2.1 CenterZ=0 NormalX=0 NormalY=0 NormalZ=1 AngleXU=0 Radius=1 StartAngle=5.49779 EndAngle=8.63938
    g62: LineSegment StartX=58.8508 StartY=-1.76552 StartZ=0 EndX=63.4234 EndY=2.80711 EndZ=0
    g63: LineSegment StartX=60.265 StartY=-3.17973 StartZ=0 EndX=64.8376 EndY=1.39289 EndZ=0
    g64: ArcOfCircle CenterX=65.5303 CenterY=-1.45 CenterZ=0 NormalX=0 NormalY=0 NormalZ=1 AngleXU=0 Radius=1 StartAngle=2.35619 EndAngle=5.49779
    g65: ArcOfCircle CenterX=71.2803 CenterY=4.3 CenterZ=0 NormalX=0 NormalY=0 NormalZ=1 AngleXU=0 Radius=1 StartAngle=5.49779 EndAngle=8.63938
    g66: LineSegment StartX=64.8232 StartY=-0.742893 StartZ=0 EndX=70.5732 EndY=5.00711 EndZ=0
    g67: LineSegment StartX=66.2374 StartY=-2.15711 StartZ=0 EndX=71.9874 EndY=3.59289 EndZ=0
    g68: ArcOfCircle CenterX=67.3 CenterY=5.26947 CenterZ=0 NormalX=0 NormalY=0 NormalZ=1 AngleXU=0 Radius=1 StartAngle=2.35619 EndAngle=5.49779
    g69: ArcOfCircle CenterX=68.0958 CenterY=6.06528 CenterZ=0 NormalX=0 NormalY=0 NormalZ=1 AngleXU=0 Radius=1 StartAngle=5.49779 EndAngle=8.63938
    g70: LineSegment StartX=66.5929 StartY=5.97657 StartZ=0 EndX=67.3887 EndY=6.77238 EndZ=0
    g71: LineSegment StartX=68.0071 StartY=4.56236 StartZ=0 EndX=68.8029 EndY=5.35817 EndZ=0
    g72: ArcOfCircle CenterX=71.33 CenterY=-0.6 CenterZ=0 NormalX=0 NormalY=0 NormalZ=1 AngleXU=0 Radius=1 StartAngle=2.35619 EndAngle=5.49779
    g73: ArcOfCircle CenterX=76.23 CenterY=4.3 CenterZ=0 NormalX=0 NormalY=0 NormalZ=1 AngleXU=0 Radius=1 StartAngle=5.49779 EndAngle=8.63938
    g74: LineSegment StartX=70.6229 StartY=0.107107 StartZ=0 EndX=75.5229 EndY=5.00711 EndZ=0
    g75: LineSegment StartX=72.0371 StartY=-1.30711 StartZ=0 EndX=76.9371 EndY=3.59289 EndZ=0
    g76: ArcOfCircle CenterX=77.1508 CenterY=0.271054 CenterZ=0 NormalX=0 NormalY=0 NormalZ=1 AngleXU=0 Radius=1 StartAngle=2.35619 EndAngle=5.49779
    g77: ArcOfCircle CenterX=81.1798 CenterY=4.3 CenterZ=0 NormalX=0 NormalY=0 NormalZ=1 AngleXU=0 Radius=1 StartAngle=5.49779 EndAngle=8.63938
    g78: LineSegment StartX=76.4437 StartY=0.978161 StartZ=0 EndX=80.4727 EndY=5.00711 EndZ=0
    g79: LineSegment StartX=77.8579 StartY=-0.436053 StartZ=0 EndX=81.8869 EndY=3.59289 EndZ=0
    g80: ArcOfCircle CenterX=82.5795 CenterY=0.75 CenterZ=0 NormalX=0 NormalY=0 NormalZ=1 AngleXU=0 Radius=1 StartAngle=2.35619 EndAngle=5.49779
    g81: ArcOfCircle CenterX=84.4617 CenterY=2.63217 CenterZ=0 NormalX=0 NormalY=0 NormalZ=1 AngleXU=0 Radius=1 StartAngle=5.49779 EndAngle=8.63938
    g82: LineSegment StartX=81.8724 StartY=1.45711 StartZ=0 EndX=83.7546 EndY=3.33928 EndZ=0
    g83: LineSegment StartX=83.2866 StartY=0.0428931 StartZ=0 EndX=85.1688 EndY=1.92507 EndZ=0
    g84: ArcOfCircle CenterX=87.6811 CenterY=0.901792 CenterZ=0 NormalX=0 NormalY=0 NormalZ=1 AngleXU=0 Radius=1 StartAngle=2.35619 EndAngle=5.49779
    g85: ArcOfCircle CenterX=93.2793 CenterY=6.5 CenterZ=0 NormalX=0 NormalY=0 NormalZ=1 AngleXU=0 Radius=1 StartAngle=5.49779 EndAngle=8.63938
    g86: LineSegment StartX=86.974 StartY=1.6089 StartZ=0 EndX=92.5722 EndY=7.20711 EndZ=0
    g87: LineSegment StartX=88.3882 StartY=0.194685 StartZ=0 EndX=93.9864 EndY=5.79289 EndZ=0
    g88: ArcOfCircle CenterX=94.2788 CenterY=2.54974 CenterZ=0 NormalX=0 NormalY=0 NormalZ=1 AngleXU=0 Radius=1 StartAngle=2.35619 EndAngle=5.49779
    g89: ArcOfCircle CenterX=98.229 CenterY=6.5 CenterZ=0 NormalX=0 NormalY=0 NormalZ=1 AngleXU=0 Radius=1 StartAngle=5.49779 EndAngle=8.63938
    g90: LineSegment StartX=93.5717 StartY=3.25685 StartZ=0 EndX=97.5219 EndY=7.20711 EndZ=0
    g91: LineSegment StartX=94.9859 StartY=1.84263 StartZ=0 EndX=98.9361 EndY=5.79289 EndZ=0
    g92: ArcOfCircle CenterX=98.1874 CenterY=1.5086 CenterZ=0 NormalX=0 NormalY=0 NormalZ=1 AngleXU=0 Radius=1 StartAngle=2.35619 EndAngle=5.49779
    g93: ArcOfCircle CenterX=103.179 CenterY=6.5 CenterZ=0 NormalX=0 NormalY=0 NormalZ=1 AngleXU=0 Radius=1 StartAngle=5.49779 EndAngle=8.63938
    g94: LineSegment StartX=97.4803 StartY=2.21571 StartZ=0 EndX=102.472 EndY=7.20711 EndZ=0
    g95: LineSegment StartX=98.8945 StartY=0.801498 StartZ=0 EndX=103.886 EndY=5.79289 EndZ=0
    g96: ArcOfCircle CenterX=-7.1 CenterY=10.0654 CenterZ=0 NormalX=0 NormalY=0 NormalZ=1 AngleXU=0 Radius=1 StartAngle=2.35619 EndAngle=5.49779
    g97: ArcOfCircle CenterX=-6.99407 CenterY=10.1714 CenterZ=0 NormalX=0 NormalY=0 NormalZ=1 AngleXU=0 Radius=1 StartAngle=5.49779 EndAngle=8.63938
    g98: LineSegment StartX=-7.80711 StartY=10.7725 StartZ=0 EndX=-7.70117 EndY=10.8785 EndZ=0
    g99: LineSegment StartX=-6.39289 StartY=9.35833 StartZ=0 EndX=-6.28696 EndY=9.46426 EndZ=0
  constraints (251):
    c: Tangent(g0,g2) = 1.5708
    c: Tangent(g0,g3) = -1.5708
    c: Tangent(g1,g2) = 1.5708
    c: Tangent(g1,g3) = -1.5708
    c: Equal(g0,g1)
    c: Angle(g-1,g2) = 0.785398
    c: Radius(g0) = 1
    c: Tangent(g4,g6) = 1.5708
    c: Tangent(g4,g7) = -1.5708
    c: Tangent(g5,g6) = 1.5708
    c: Tangent(g5,g7) = -1.5708
    c: Equal(g4,g5)
    c: Angle(g-1,g6) = 0.785398
    c: Radius(g4) = 1
    c: Distance(g6,g3) = 1.5
    c: Distance(g1,g-3) = 1.5
    c: Distance(g5,g-3) = 1.5
    c: Distance(g4,g-4) = 1.5
    c: Distance(g4,g-5) = 1.5
    c: Distance(g0,g-6) = 1.5
    c: Tangent(g8,g10) = 1.5708
    c: Tangent(g8,g11) = -1.5708
    c: Tangent(g9,g10) = 1.5708
    c: Tangent(g9,g11) = -1.5708
    c: Equal(g8,g9)
    c: Angle(g-1,g10) = 0.785398
    c: Radius(g8) = 1
    c: Tangent(g12,g14) = 1.5708
    c: Tangent(g12,g15) = -1.5708
    c: Tangent(g13,g14) = 1.5708
    c: Tangent(g13,g15) = -1.5708
    c: Equal(g12,g13)
    c: Angle(g-1,g14) = 0.785398
    c: Radius(g12) = 1
    c: Tangent(g16,g18) = 1.5708
    c: Tangent(g16,g19) = -1.5708
    c: Tangent(g17,g18) = 1.5708
    c: Tangent(g17,g19) = -1.5708
    c: Equal(g16,g17)
    c: Angle(g-1,g18) = 0.785398
    c: Radius(g16) = 1
    c: Distance(g7,g10) = 1.5
    c: Distance(g8,g-5) = 1.5
    c: Distance(g11,g14) = 1.5
    c: Distance(g18,g15) = 1.5
    c: Distance(g9,g-7) = 0.0001
    c: Distance(g13,g-7) = 0.0001
    c: Distance(g12,g-8) = 1.5
    c: Radius(g-9) = 0.5
    c: Distance(g16,g-9) = 1.5
    c: Distance(g17,g-10) = 1.5
    c: Tangent(g20,g22) = 1.5708
    c: Tangent(g20,g23) = -1.5708
    c: Tangent(g21,g22) = 1.5708
    c: Tangent(g21,g23) = -1.5708
    c: Equal(g20,g21)
    c: Angle(g-1,g22) = 0.785398
    c: Radius(g20) = 1
    c: Tangent(g24,g26) = 1.5708
    c: Tangent(g24,g27) = -1.5708
    c: Tangent(g25,g26) = 1.5708
    c: Tangent(g25,g27) = -1.5708
    c: Equal(g24,g25)
    c: Angle(g-1,g26) = 0.785398
    c: Radius(g24) = 1
    c: Distance(g19,g22) = 1.5
    c: Distance(g26,g23) = 1.5
    c: Distance(g21,g-10) = 1.5
    c: Distance(g24,g-12) = 1.5
    c: Distance(g25,g-10) = 1.5
    c: Distance(g-12,g20) = 1.5
    c: Tangent(g28,g30) = 1.5708
    c: Tangent(g28,g31) = -1.5708
    c: Tangent(g29,g30) = 1.5708
    c: Tangent(g29,g31) = -1.5708
    c: Equal(g28,g29)
    c: Angle(g-1,g30) = 0.785398
    c: Radius(g28) = 1
    c: Distance(g28,g-15) = 1.5
    c: Distance(g29,g-14) = 1.5
    c: Distance(g27,g30) = 1.5
    c: Tangent(g32,g34) = 1.5708
    c: Tangent(g32,g35) = -1.5708
    c: Tangent(g33,g34) = 1.5708
    c: Tangent(g33,g35) = -1.5708
    c: Equal(g32,g33)
    c: Angle(g-1,g34) = 0.785398
    c: Radius(g32) = 1
    c: Distance(g34,g31) = 1.5
    c: Distance(g-14,g33) = 1.5
    c: Distance(g32,g-16) = 1.5
    c: Tangent(g36,g38) = 1.5708
    c: Tangent(g36,g39) = -1.5708
    c: Tangent(g37,g38) = 1.5708
    c: Tangent(g37,g39) = -1.5708
    c: Equal(g36,g37)
    c: Angle(g-1,g38) = 0.785398
    c: Radius(g36) = 1
    c: Tangent(g40,g42) = 1.5708
    c: Tangent(g40,g43) = -1.5708
    c: Tangent(g41,g42) = 1.5708
    c: Tangent(g41,g43) = -1.5708
    c: Equal(g40,g41)
    c: Angle(g-1,g42) = 0.785398
    c: Radius(g40) = 1
    c: Tangent(g44,g46) = 1.5708
    c: Tangent(g44,g47) = -1.5708
    c: Tangent(g45,g46) = 1.5708
    c: Tangent(g45,g47) = -1.5708
    c: Equal(g44,g45)
    c: Angle(g-1,g46) = 0.785398
    c: Radius(g44) = 1
    c: Distance(g35,g38) = 1.5
    c: Distance(g42,g39) = 1.5
    c: Distance(g46,g43) = 1.5
    c: Tangent(g48,g50) = 1.5708
    c: Tangent(g48,g51) = -1.5708
    c: Tangent(g49,g50) = 1.5708
    c: Tangent(g49,g51) = -1.5708
    c: Equal(g48,g49)
    c: Angle(g-1,g50) = 0.785398
    c: Radius(g48) = 1
    c: Distance(g47,g50) = 1.5
    c: Tangent(g52,g54) = 1.5708
    c: Tangent(g52,g55) = -1.5708
    c: Tangent(g53,g54) = 1.5708
    c: Tangent(g53,g55) = -1.5708
    c: Equal(g52,g53)
    c: Angle(g-1,g54) = 0.785398
    c: Radius(g52) = 1
    c: Distance(g51,g54) = 1.5
    c: Distance(g37,g-17) = 1.5
    c: Distance(g41,g-17) = 1.5
    c: Distance(g-25,g45) = 1.5
    c: Distance(g36,g-21) = 1.5
    c: Distance(g40,g-18) = 1.5
    c: Distance(g44,g-18) = 1.5
    c: Distance(g48,g-19) = 1.5
    c: Distance(g49,g-22) = 1.5
    c: Distance(g52,g-20) = 1.5
    c: Distance(g53,g-24) = 1.5
    c: Tangent(g56,g58) = 1.5708
    c: Tangent(g56,g59) = -1.5708
    c: Tangent(g57,g58) = 1.5708
    c: Tangent(g57,g59) = -1.5708
    c: Equal(g56,g57)
    c: Angle(g-1,g58) = 0.785398
    c: Radius(g56) = 1
    c: Tangent(g60,g62) = 1.5708
    c: Tangent(g60,g63) = -1.5708
    c: Tangent(g61,g62) = 1.5708
    c: Tangent(g61,g63) = -1.5708
    c: Equal(g60,g61)
    c: Angle(g-1,g62) = 0.785398
    c: Radius(g60) = 1
    c: Tangent(g64,g66) = 1.5708
    c: Tangent(g64,g67) = -1.5708
    c: Tangent(g65,g66) = 1.5708
    c: Tangent(g65,g67) = -1.5708
    c: Equal(g64,g65)
    c: Angle(g-1,g66) = 0.785398
    c: Radius(g64) = 1
    c: Distance(g55,g58) = 1.5
    c: Distance(g62,g59) = 1.5
    c: Distance(g66,g63) = 1.5
    c: Distance(g56,g-26) = 1.5
    c: Distance(g60,g-27) = 1.5
    c: Distance(g57,g-24) = 1.5
    c: Distance(g61,g-24) = 1.5
    c: Distance(g64,g-28) = 1.5
    c: Distance(g65,g-31) = 1.5
    c: Tangent(g68,g70) = 1.5708
    c: Tangent(g68,g71) = -1.5708
    c: Tangent(g69,g70) = 1.5708
    c: Tangent(g69,g71) = -1.5708
    c: Equal(g68,g69)
    c: Angle(g-1,g70) = 0.785398
    c: Radius(g68) = 1
    c: Distance(g66,g71) = 1.5
    c: Distance(g-29,g69) = 1.5
    c: Distance(g68,g-32) = 1.5
    c: Tangent(g72,g74) = 1.5708
    c: Tangent(g72,g75) = -1.5708
    c: Tangent(g73,g74) = 1.5708
    c: Tangent(g73,g75) = -1.5708
    c: Equal(g72,g73)
    c: Angle(g-1,g74) = 0.785398
    c: Radius(g72) = 1
    c: Tangent(g76,g78) = 1.5708
    c: Tangent(g76,g79) = -1.5708
    c: Tangent(g77,g78) = 1.5708
    c: Tangent(g77,g79) = -1.5708
    c: Equal(g76,g77)
    c: Angle(g-1,g78) = 0.785398
    c: Radius(g76) = 1
    c: Tangent(g80,g82) = 1.5708
    c: Tangent(g80,g83) = -1.5708
    c: Tangent(g81,g82) = 1.5708
    c: Tangent(g81,g83) = -1.5708
    c: Equal(g80,g81)
    c: Angle(g-1,g82) = 0.785398
    c: Radius(g80) = 1
    c: Distance(g67,g74) = 1.5
    c: Distance(g78,g75) = 1.5
    c: Distance(g79,g82) = 1.5
    c: Distance(g72,g-33) = 1.5
    c: Distance(g73,g-31) = 1.5
    c: Distance(g77,g-31) = 1.5
    c: Distance(g76,g-34) = 1.5
    c: Distance(g80,g-35) = 1.5
    c: Distance(g81,g-36) = 0.1
    c: Tangent(g84,g86) = 1.5708
    c: Tangent(g84,g87) = -1.5708
    c: Tangent(g85,g86) = 1.5708
    c: Tangent(g85,g87) = -1.5708
    c: Equal(g84,g85)
    c: Angle(g-1,g86) = 0.785398
    c: Radius(g84) = 1
    c: Tangent(g88,g90) = 1.5708
    c: Tangent(g88,g91) = -1.5708
    c: Tangent(g89,g90) = 1.5708
    c: Tangent(g89,g91) = -1.5708
    c: Equal(g88,g89)
    c: Angle(g-1,g90) = 0.785398
    c: Radius(g88) = 1
    c: Tangent(g92,g94) = 1.5708
    c: Tangent(g92,g95) = -1.5708
    c: Tangent(g93,g94) = 1.5708
    c: Tangent(g93,g95) = -1.5708
    c: Equal(g92,g93)
    c: Angle(g-1,g94) = 0.785398
    c: Radius(g92) = 1
    c: Distance(g83,g86) = 1.5
    c: Distance(g90,g87) = 1.5
    c: Distance(g91,g94) = 1.5
    c: Distance(g84,g-40) = 1.5
    c: Distance(g88,g-38) = 1.5
    c: Distance(g85,g-37) = 1.5
    c: Distance(g89,g-37) = 1.5
    c: Distance(g93,g-37) = 1.5
    c: Distance(g92,g-38) = 1.5
    c: Tangent(g96,g98) = 1.5708
    c: Tangent(g96,g99) = -1.5708
    c: Tangent(g97,g98) = 1.5708
    c: Tangent(g97,g99) = -1.5708
    c: Equal(g96,g97)
    c: Angle(g-1,g98) = 0.785398
    c: Radius(g96) = 1
    c: Distance(g-41,g97) = 1.4
    c: Distance(g2,g99) = 1.5
    c: Distance(g96,g-6) = 1.4
FEATURE [PartDesign::Pocket] Pocket001
  BaseFeature = -> Pad002
  Direction = (0,0,1)
  Length = 5
  Length2 = 5
  Profile = -> Sketch005
  ReferenceAxis = -> Sketch005 [N_Axis]
  Suppressed = false
  Type = 0
FEATURE [PartDesign::LinearPattern] LinearPattern001
  BaseFeature = -> Pocket001
  Direction = -> Sketch005 [V_Axis]
  Length = 19
  Mode = 1
  Occurrences = 2
  Offset = 19
  Originals = -> [Pocket001]
  Suppressed = false
FEATURE [Sketcher::SketchObject] Sketch006
  AttachmentSupport = -> [LinearPattern001]
  ExternalGeometry = -> [LinearPattern001]
  FullyConstrained = true
  MapMode = 5
  Placement = pos=(0,0,0) rot=(1,0,0;3.14159rad)
  sketch-geometry (172):
    g0: ArcOfCircle CenterX=-7 CenterY=43.2157 CenterZ=0 NormalX=0 NormalY=0 NormalZ=1 AngleXU=0 Radius=1 StartAngle=2.35619 EndAngle=5.49779
    g1: ArcOfCircle CenterX=-5.21569 CenterY=45 CenterZ=0 NormalX=0 NormalY=0 NormalZ=1 AngleXU=0 Radius=1 StartAngle=5.49779 EndAngle=8.63938
    g2: LineSegment StartX=-7.70711 StartY=43.9228 StartZ=0 EndX=-5.9228 EndY=45.7071 EndZ=0
    g3: LineSegment StartX=-6.29289 StartY=42.5086 StartZ=0 EndX=-4.50858 EndY=44.2929 EndZ=0
    g4: ArcOfCircle CenterX=-3.06594 CenterY=42.2 CenterZ=0 NormalX=0 NormalY=0 NormalZ=1 AngleXU=0 Radius=1 StartAngle=2.35619 EndAngle=5.49779
    g5: ArcOfCircle CenterX=-0.265941 CenterY=45 CenterZ=0 NormalX=0 NormalY=0 NormalZ=1 AngleXU=0 Radius=1 StartAngle=5.49779 EndAngle=8.63938
    g6: LineSegment StartX=-3.77305 StartY=42.9071 StartZ=0 EndX=-0.973048 EndY=45.7071 EndZ=0
    g7: LineSegment StartX=-2.35884 StartY=41.4929 StartZ=0 EndX=0.441166 EndY=44.2929 EndZ=0
    g8: ArcOfCircle CenterX=2.33172 CenterY=42.6479 CenterZ=0 NormalX=0 NormalY=0 NormalZ=1 AngleXU=0 Radius=1 StartAngle=2.35619 EndAngle=5.49779
    g9: ArcOfCircle CenterX=4.68381 CenterY=45 CenterZ=0 NormalX=0 NormalY=0 NormalZ=1 AngleXU=0 Radius=1 StartAngle=5.49779 EndAngle=8.63938
    g10: LineSegment StartX=1.62461 StartY=43.355 StartZ=0 EndX=3.9767 EndY=45.7071 EndZ=0
    g11: LineSegment StartX=3.03883 StartY=41.9408 StartZ=0 EndX=5.39091 EndY=44.2929 EndZ=0
    g12: ArcOfCircle CenterX=8.18356 CenterY=43.55 CenterZ=0 NormalX=0 NormalY=0 NormalZ=1 AngleXU=0 Radius=1 StartAngle=2.35619 EndAngle=5.49779
    g13: ArcOfCircle CenterX=9.63356 CenterY=45 CenterZ=0 NormalX=0 NormalY=0 NormalZ=1 AngleXU=0 Radius=1 StartAngle=5.49779 EndAngle=8.63938
    g14: LineSegment StartX=7.47645 StartY=44.2571 StartZ=0 EndX=8.92645 EndY=45.7071 EndZ=0
    g15: LineSegment StartX=8.89066 StartY=42.8429 StartZ=0 EndX=10.3407 EndY=44.2929 EndZ=0
    g16: ArcOfCircle CenterX=11.3237 CenterY=42.4475 CenterZ=0 NormalX=0 NormalY=0 NormalZ=1 AngleXU=0 Radius=1 StartAngle=2.35619 EndAngle=5.49779
    g17: ArcOfCircle CenterX=13.8762 CenterY=45 CenterZ=0 NormalX=0 NormalY=0 NormalZ=1 AngleXU=0 Radius=1 StartAngle=5.49779 EndAngle=8.63938
    g18: LineSegment StartX=10.6166 StartY=43.1546 StartZ=0 EndX=13.1691 EndY=45.7071 EndZ=0
    g19: LineSegment StartX=12.0308 StartY=41.7404 StartZ=0 EndX=14.5833 EndY=44.2929 EndZ=0
    g20: ArcOfCircle CenterX=16.2212 CenterY=42.3953 CenterZ=0 NormalX=0 NormalY=0 NormalZ=1 AngleXU=0 Radius=1 StartAngle=2.35619 EndAngle=5.49779
    g21: ArcOfCircle CenterX=18.8259 CenterY=45 CenterZ=0 NormalX=0 NormalY=0 NormalZ=1 AngleXU=0 Radius=1 StartAngle=5.49779 EndAngle=8.63938
    g22: LineSegment StartX=15.5141 StartY=43.1024 StartZ=0 EndX=18.1188 EndY=45.7071 EndZ=0
    g23: LineSegment StartX=16.9283 StartY=41.6881 StartZ=0 EndX=19.5331 EndY=44.2929 EndZ=0
    g24: ArcOfCircle CenterX=21.3926 CenterY=42.6169 CenterZ=0 NormalX=0 NormalY=0 NormalZ=1 AngleXU=0 Radius=1 StartAngle=2.35619 EndAngle=5.49779
    g25: ArcOfCircle CenterX=23.7757 CenterY=45 CenterZ=0 NormalX=0 NormalY=0 NormalZ=1 AngleXU=0 Radius=1 StartAngle=5.49779 EndAngle=8.63938
    g26: LineSegment StartX=20.6855 StartY=43.324 StartZ=0 EndX=23.0686 EndY=45.7071 EndZ=0
    g27: LineSegment StartX=22.0997 StartY=41.9098 StartZ=0 EndX=24.4828 EndY=44.2929 EndZ=0
    g28: ArcOfCircle CenterX=27.2754 CenterY=43.55 CenterZ=0 NormalX=0 NormalY=0 NormalZ=1 AngleXU=0 Radius=1 StartAngle=2.35619 EndAngle=5.49779
    g29: ArcOfCircle CenterX=28.7254 CenterY=45 CenterZ=0 NormalX=0 NormalY=0 NormalZ=1 AngleXU=0 Radius=1 StartAngle=5.49779 EndAngle=8.63938
    g30: LineSegment StartX=26.5683 StartY=44.2571 StartZ=0 EndX=28.0183 EndY=45.7071 EndZ=0
    g31: LineSegment StartX=27.9825 StartY=42.8429 StartZ=0 EndX=29.4325 EndY=44.2929 EndZ=0
    g32: ArcOfCircle CenterX=30.6435 CenterY=41.9683 CenterZ=0 NormalX=0 NormalY=0 NormalZ=1 AngleXU=0 Radius=1 StartAngle=2.35619 EndAngle=5.49779
    g33: ArcOfCircle CenterX=35.8725 CenterY=47.1973 CenterZ=0 NormalX=0 NormalY=0 NormalZ=1 AngleXU=0 Radius=1 StartAngle=5.49779 EndAngle=8.63938
    g34: LineSegment StartX=29.9364 StartY=42.6755 StartZ=0 EndX=35.1654 EndY=47.9044 EndZ=0
    g35: LineSegment StartX=31.3506 StartY=41.2612 StartZ=0 EndX=36.5796 EndY=46.4902 EndZ=0
    g36: ArcOfCircle CenterX=31.8017 CenterY=48.0762 CenterZ=0 NormalX=0 NormalY=0 NormalZ=1 AngleXU=0 Radius=1 StartAngle=2.35619 EndAngle=5.49779
    g37: ArcOfCircle CenterX=35.7 CenterY=51.9746 CenterZ=0 NormalX=0 NormalY=0 NormalZ=1 AngleXU=0 Radius=1 StartAngle=5.49779 EndAngle=8.63938
    g38: LineSegment StartX=31.0946 StartY=48.7833 StartZ=0 EndX=34.9929 EndY=52.6817 EndZ=0
    g39: LineSegment StartX=32.5088 StartY=47.3691 StartZ=0 EndX=36.4071 EndY=51.2674 EndZ=0
    g40: ArcOfCircle CenterX=39.5014 CenterY=55.7759 CenterZ=0 NormalX=0 NormalY=0 NormalZ=1 AngleXU=0 Radius=1 StartAngle=2.35619 EndAngle=5.49779
    g41: ArcOfCircle CenterX=43.1254 CenterY=59.4 CenterZ=0 NormalX=0 NormalY=0 NormalZ=1 AngleXU=0 Radius=1 StartAngle=5.49779 EndAngle=8.63938
    g42: LineSegment StartX=38.7943 StartY=56.483 StartZ=0 EndX=42.4183 EndY=60.1071 EndZ=0
    g43: LineSegment StartX=40.2085 StartY=55.0688 StartZ=0 EndX=43.8326 EndY=58.6929 EndZ=0
    g44: ArcOfCircle CenterX=31 CenterY=37.3751 CenterZ=0 NormalX=0 NormalY=0 NormalZ=1 AngleXU=0 Radius=1 StartAngle=2.35619 EndAngle=5.49779
    g45: ArcOfCircle CenterX=38.5822 CenterY=44.9572 CenterZ=0 NormalX=0 NormalY=0 NormalZ=1 AngleXU=0 Radius=1 StartAngle=5.49779 EndAngle=8.63938
    g46: LineSegment StartX=30.2929 StartY=38.0822 StartZ=0 EndX=37.8751 EndY=45.6643 EndZ=0
    g47: LineSegment StartX=31.7071 StartY=36.668 StartZ=0 EndX=39.2893 EndY=44.2501 EndZ=0
    g48: ArcOfCircle CenterX=36.8447 CenterY=38.27 CenterZ=0 NormalX=0 NormalY=0 NormalZ=1 AngleXU=0 Radius=1 StartAngle=2.35619 EndAngle=5.49779
    g49: ArcOfCircle CenterX=41.3451 CenterY=42.7704 CenterZ=0 NormalX=0 NormalY=0 NormalZ=1 AngleXU=0 Radius=1 StartAngle=5.49779 EndAngle=8.63938
    g50: LineSegment StartX=36.1376 StartY=38.9772 StartZ=0 EndX=40.638 EndY=43.4775 EndZ=0
    g51: LineSegment StartX=37.5518 StartY=37.5629 StartZ=0 EndX=42.0522 EndY=42.0633 EndZ=0
    g52: ArcOfCircle CenterX=40.9834 CenterY=37.459 CenterZ=0 NormalX=0 NormalY=0 NormalZ=1 AngleXU=0 Radius=1 StartAngle=2.35619 EndAngle=5.49779
    g53: ArcOfCircle CenterX=46.0244 CenterY=42.5 CenterZ=0 NormalX=0 NormalY=0 NormalZ=1 AngleXU=0 Radius=1 StartAngle=5.49779 EndAngle=8.63938
    g54: LineSegment StartX=40.2763 StartY=38.1661 StartZ=0 EndX=45.3173 EndY=43.2071 EndZ=0
    g55: LineSegment StartX=41.6905 StartY=36.7519 StartZ=0 EndX=46.7315 EndY=41.7929 EndZ=0
    g56: ArcOfCircle CenterX=47.2242 CenterY=38.75 CenterZ=0 NormalX=0 NormalY=0 NormalZ=1 AngleXU=0 Radius=1 StartAngle=2.35619 EndAngle=5.49779
    g57: ArcOfCircle CenterX=50.9742 CenterY=42.5 CenterZ=0 NormalX=0 NormalY=0 NormalZ=1 AngleXU=0 Radius=1 StartAngle=5.49779 EndAngle=8.63938
    g58: LineSegment StartX=46.5171 StartY=39.4571 StartZ=0 EndX=50.2671 EndY=43.2071 EndZ=0
    g59: LineSegment StartX=47.9313 StartY=38.0429 StartZ=0 EndX=51.6813 EndY=41.7929 EndZ=0
    g60: ArcOfCircle CenterX=50 CenterY=36.5761 CenterZ=0 NormalX=0 NormalY=0 NormalZ=1 AngleXU=0 Radius=1 StartAngle=2.35619 EndAngle=5.49779
    g61: ArcOfCircle CenterX=54.2571 CenterY=40.8332 CenterZ=0 NormalX=0 NormalY=0 NormalZ=1 AngleXU=0 Radius=1 StartAngle=5.49779 EndAngle=8.63938
    g62: LineSegment StartX=49.2929 StartY=37.2832 StartZ=0 EndX=53.55 EndY=41.5403 EndZ=0
    g63: LineSegment StartX=50.7071 StartY=35.869 StartZ=0 EndX=54.9642 EndY=40.126 EndZ=0
    g64: ArcOfCircle CenterX=53.5737 CenterY=35.2 CenterZ=0 NormalX=0 NormalY=0 NormalZ=1 AngleXU=0 Radius=1 StartAngle=2.35619 EndAngle=5.49779
    g65: ArcOfCircle CenterX=60.9756 CenterY=42.6019 CenterZ=0 NormalX=0 NormalY=0 NormalZ=1 AngleXU=0 Radius=1 StartAngle=5.49779 EndAngle=8.63938
    g66: LineSegment StartX=52.8666 StartY=35.9071 StartZ=0 EndX=60.2685 EndY=43.309 EndZ=0
    g67: LineSegment StartX=54.2808 StartY=34.4929 StartZ=0 EndX=61.6827 EndY=41.8948 EndZ=0
    g68: ArcOfCircle CenterX=59.0865 CenterY=35.763 CenterZ=0 NormalX=0 NormalY=0 NormalZ=1 AngleXU=0 Radius=1 StartAngle=2.35619 EndAngle=5.49779
    g69: ArcOfCircle CenterX=65.8234 CenterY=42.5 CenterZ=0 NormalX=0 NormalY=0 NormalZ=1 AngleXU=0 Radius=1 StartAngle=5.49779 EndAngle=8.63938
    g70: LineSegment StartX=58.3794 StartY=36.4702 StartZ=0 EndX=65.1163 EndY=43.2071 EndZ=0
    g71: LineSegment StartX=59.7936 StartY=35.0559 StartZ=0 EndX=66.5305 EndY=41.7929 EndZ=0
    g72: ArcOfCircle CenterX=64.8232 CenterY=36.55 CenterZ=0 NormalX=0 NormalY=0 NormalZ=1 AngleXU=0 Radius=1 StartAngle=2.35619 EndAngle=5.49779
    g73: ArcOfCircle CenterX=70.7732 CenterY=42.5 CenterZ=0 NormalX=0 NormalY=0 NormalZ=1 AngleXU=0 Radius=1 StartAngle=5.49779 EndAngle=8.63938
    g74: LineSegment StartX=64.1161 StartY=37.2571 StartZ=0 EndX=70.0661 EndY=43.2071 EndZ=0
    g75: LineSegment StartX=65.5303 StartY=35.8429 StartZ=0 EndX=71.4803 EndY=41.7929 EndZ=0
    g76: ArcOfCircle CenterX=70.6042 CenterY=37.3813 CenterZ=0 NormalX=0 NormalY=0 NormalZ=1 AngleXU=0 Radius=1 StartAngle=2.35619 EndAngle=5.49779
    g77: ArcOfCircle CenterX=79.3593 CenterY=46.1364 CenterZ=0 NormalX=0 NormalY=0 NormalZ=1 AngleXU=0 Radius=1 StartAngle=5.49779 EndAngle=8.63938
    g78: LineSegment StartX=69.8971 StartY=38.0884 StartZ=0 EndX=78.6522 EndY=46.8435 EndZ=0
    g79: LineSegment StartX=71.3113 StartY=36.6742 StartZ=0 EndX=80.0665 EndY=45.4293 EndZ=0
    g80: ArcOfCircle CenterX=76.5441 CenterY=38.3715 CenterZ=0 NormalX=0 NormalY=0 NormalZ=1 AngleXU=0 Radius=1 StartAngle=2.35619 EndAngle=5.49779
    g81: ArcOfCircle CenterX=82.8755 CenterY=44.7028 CenterZ=0 NormalX=0 NormalY=0 NormalZ=1 AngleXU=0 Radius=1 StartAngle=5.49779 EndAngle=8.63938
    g82: LineSegment StartX=75.837 StartY=39.0786 StartZ=0 EndX=82.1684 EndY=45.4099 EndZ=0
    g83: LineSegment StartX=77.2512 StartY=37.6643 StartZ=0 EndX=83.5826 EndY=43.9957 EndZ=0
    g84: ArcOfCircle CenterX=81.8724 CenterY=38.75 CenterZ=0 NormalX=0 NormalY=0 NormalZ=1 AngleXU=0 Radius=1 StartAngle=2.35619 EndAngle=5.49779
    g85: ArcOfCircle CenterX=88.3928 CenterY=45.2704 CenterZ=0 NormalX=0 NormalY=0 NormalZ=1 AngleXU=0 Radius=1 StartAngle=5.49779 EndAngle=8.63938
    g86: LineSegment StartX=81.1653 StartY=39.4571 StartZ=0 EndX=87.6857 EndY=45.9775 EndZ=0
    g87: LineSegment StartX=82.5795 StartY=38.0429 StartZ=0 EndX=89.0999 EndY=44.5633 EndZ=0
    g88: ArcOfCircle CenterX=86.449 CenterY=38.3769 CenterZ=0 NormalX=0 NormalY=0 NormalZ=1 AngleXU=0 Radius=1 StartAngle=2.35619 EndAngle=5.49779
    g89: ArcOfCircle CenterX=95.1543 CenterY=47.0821 CenterZ=0 NormalX=0 NormalY=0 NormalZ=1 AngleXU=0 Radius=1 StartAngle=5.49779 EndAngle=8.63938
    g90: LineSegment StartX=85.7419 StartY=39.084 StartZ=0 EndX=94.4472 EndY=47.7892 EndZ=0
    g91: LineSegment StartX=87.1561 StartY=37.6697 StartZ=0 EndX=95.8614 EndY=46.375 EndZ=0
    g92: ArcOfCircle CenterX=93.3548 CenterY=40.3329 CenterZ=0 NormalX=0 NormalY=0 NormalZ=1 AngleXU=0 Radius=1 StartAngle=2.35619 EndAngle=5.49779
    g93: ArcOfCircle CenterX=98.9105 CenterY=45.8885 CenterZ=0 NormalX=0 NormalY=0 NormalZ=1 AngleXU=0 Radius=1 StartAngle=5.49779 EndAngle=8.63938
    g94: LineSegment StartX=92.6477 StartY=41.04 StartZ=0 EndX=98.2034 EndY=46.5957 EndZ=0
    g95: LineSegment StartX=94.0619 StartY=39.6258 StartZ=0 EndX=99.6176 EndY=45.1814 EndZ=0
    g96: ArcOfCircle CenterX=97.7715 CenterY=39.7999 CenterZ=0 NormalX=0 NormalY=0 NormalZ=1 AngleXU=0 Radius=1 StartAngle=2.35619 EndAngle=5.49779
    g97: ArcOfCircle CenterX=102.645 CenterY=44.6729 CenterZ=0 NormalX=0 NormalY=0 NormalZ=1 AngleXU=0 Radius=1 StartAngle=5.49779 EndAngle=8.63938
    g98: LineSegment StartX=97.0644 StartY=40.507 StartZ=0 EndX=101.937 EndY=45.38 EndZ=0
    g99: LineSegment StartX=98.4786 StartY=39.0927 StartZ=0 EndX=103.352 EndY=43.9658 EndZ=0
    g100: ArcOfCircle CenterX=103.871 CenterY=40.95 CenterZ=0 NormalX=0 NormalY=0 NormalZ=1 AngleXU=0 Radius=1 StartAngle=2.35619 EndAngle=5.49779
    g101: ArcOfCircle CenterX=110.363 CenterY=47.4412 CenterZ=0 NormalX=0 NormalY=0 NormalZ=1 AngleXU=0 Radius=1 StartAngle=5.49779 EndAngle=8.63938
    g102: LineSegment StartX=103.164 StartY=41.6571 StartZ=0 EndX=109.656 EndY=48.1483 EndZ=0
    g103: LineSegment StartX=104.579 StartY=40.2429 StartZ=0 EndX=111.07 EndY=46.7341 EndZ=0
    g104: ArcOfCircle CenterX=99.0064 CenterY=50.9342 CenterZ=0 NormalX=0 NormalY=0 NormalZ=1 AngleXU=0 Radius=1 StartAngle=2.35619 EndAngle=5.49779
    g105: ArcOfCircle CenterX=101.374 CenterY=53.3017 CenterZ=0 NormalX=0 NormalY=0 NormalZ=1 AngleXU=0 Radius=1 StartAngle=5.49779 EndAngle=8.63938
    g106: LineSegment StartX=98.2993 StartY=51.6413 StartZ=0 EndX=100.667 EndY=54.0088 EndZ=0
    g107: LineSegment StartX=99.7135 StartY=50.2271 StartZ=0 EndX=102.081 EndY=52.5946 EndZ=0
    g108: ArcOfCircle CenterX=46.2157 CenterY=57.5405 CenterZ=0 NormalX=0 NormalY=0 NormalZ=1 AngleXU=0 Radius=1 StartAngle=2.35619 EndAngle=5.49779
    g109: ArcOfCircle CenterX=48.0752 CenterY=59.4 CenterZ=0 NormalX=0 NormalY=0 NormalZ=1 AngleXU=0 Radius=1 StartAngle=5.49779 EndAngle=8.63938
    g110: LineSegment StartX=45.5086 StartY=58.2476 StartZ=0 EndX=47.3681 EndY=60.1071 EndZ=0
    g111: LineSegment StartX=46.9228 StartY=56.8334 StartZ=0 EndX=48.7823 EndY=58.6929 EndZ=0
    g112: ArcOfCircle CenterX=50.157 CenterY=56.532 CenterZ=0 NormalX=0 NormalY=0 NormalZ=1 AngleXU=0 Radius=1 StartAngle=2.35619 EndAngle=5.49779
    g113: ArcOfCircle CenterX=53.0249 CenterY=59.4 CenterZ=0 NormalX=0 NormalY=0 NormalZ=1 AngleXU=0 Radius=1 StartAngle=5.49779 EndAngle=8.63938
    g114: LineSegment StartX=49.4499 StartY=57.2391 StartZ=0 EndX=52.3178 EndY=60.1071 EndZ=0
    g115: LineSegment StartX=50.8641 StartY=55.8249 StartZ=0 EndX=53.732 EndY=58.6929 EndZ=0
    g116: ArcOfCircle CenterX=56.5247 CenterY=57.95 CenterZ=0 NormalX=0 NormalY=0 NormalZ=1 AngleXU=0 Radius=1 StartAngle=2.35619 EndAngle=5.49779
    g117: ArcOfCircle CenterX=57.9747 CenterY=59.4 CenterZ=0 NormalX=0 NormalY=0 NormalZ=1 AngleXU=0 Radius=1 StartAngle=5.49779 EndAngle=8.63938
    g118: LineSegment StartX=55.8176 StartY=58.6571 StartZ=0 EndX=57.2676 EndY=60.1071 EndZ=0
    g119: LineSegment StartX=57.2318 StartY=57.2429 StartZ=0 EndX=58.6818 EndY=58.6929 EndZ=0
    g120: ArcOfCircle CenterX=60.0048 CenterY=56.4804 CenterZ=0 NormalX=0 NormalY=0 NormalZ=1 AngleXU=0 Radius=1 StartAngle=2.35619 EndAngle=5.49779
    g121: ArcOfCircle CenterX=62.9244 CenterY=59.4 CenterZ=0 NormalX=0 NormalY=0 NormalZ=1 AngleXU=0 Radius=1 StartAngle=5.49779 EndAngle=8.63938
    g122: LineSegment StartX=59.2977 StartY=57.1875 StartZ=0 EndX=62.2173 EndY=60.1071 EndZ=0
    g123: LineSegment StartX=60.7119 StartY=55.7733 StartZ=0 EndX=63.6315 EndY=58.6929 EndZ=0
    g124: ArcOfCircle CenterX=66.0737 CenterY=57.5995 CenterZ=0 NormalX=0 NormalY=0 NormalZ=1 AngleXU=0 Radius=1 StartAngle=2.35619 EndAngle=5.49779
    g125: ArcOfCircle CenterX=67.914 CenterY=59.4398 CenterZ=0 NormalX=0 NormalY=0 NormalZ=1 AngleXU=0 Radius=1 StartAngle=5.49779 EndAngle=8.63938
    g126: LineSegment StartX=65.3666 StartY=58.3066 StartZ=0 EndX=67.2069 EndY=60.1469 EndZ=0
    g127: LineSegment StartX=66.7808 StartY=56.8924 StartZ=0 EndX=68.6211 EndY=58.7327 EndZ=0
    g128: ArcOfCircle CenterX=69.5879 CenterY=56.1639 CenterZ=0 NormalX=0 NormalY=0 NormalZ=1 AngleXU=0 Radius=1 StartAngle=2.35619 EndAngle=5.49779
    g129: ArcOfCircle CenterX=73.216 CenterY=59.7921 CenterZ=0 NormalX=0 NormalY=0 NormalZ=1 AngleXU=0 Radius=1 StartAngle=5.49779 EndAngle=8.63938
    g130: LineSegment StartX=68.8808 StartY=56.871 StartZ=0 EndX=72.5089 EndY=60.4992 EndZ=0
    g131: LineSegment StartX=70.295 StartY=55.4568 StartZ=0 EndX=73.9231 EndY=59.085 EndZ=0
    g132: ArcOfCircle CenterX=76.1106 CenterY=57.7369 CenterZ=0 NormalX=0 NormalY=0 NormalZ=1 AngleXU=0 Radius=1 StartAngle=2.35619 EndAngle=5.49779
    g133: ArcOfCircle CenterX=78.9646 CenterY=60.5909 CenterZ=0 NormalX=0 NormalY=0 NormalZ=1 AngleXU=0 Radius=1 StartAngle=5.49779 EndAngle=8.63938
    g134: LineSegment StartX=75.4035 StartY=58.444 StartZ=0 EndX=78.2575 EndY=61.298 EndZ=0
    g135: LineSegment StartX=76.8177 StartY=57.0298 StartZ=0 EndX=79.6717 EndY=59.8838 EndZ=0
    g136: ArcOfCircle CenterX=81.2873 CenterY=57.9639 CenterZ=0 NormalX=0 NormalY=0 NormalZ=1 AngleXU=0 Radius=1 StartAngle=2.35619 EndAngle=5.49779
    g137: ArcOfCircle CenterX=85.3188 CenterY=61.9954 CenterZ=0 NormalX=0 NormalY=0 NormalZ=1 AngleXU=0 Radius=1 StartAngle=5.49779 EndAngle=8.63938
    g138: LineSegment StartX=80.5802 StartY=58.671 StartZ=0 EndX=84.6117 EndY=62.7025 EndZ=0
    g139: LineSegment StartX=81.9944 StartY=57.2567 StartZ=0 EndX=86.0259 EndY=61.2883 EndZ=0
    g140: ArcOfCircle CenterX=88.5064 CenterY=60.2332 CenterZ=0 NormalX=0 NormalY=0 NormalZ=1 AngleXU=0 Radius=1 StartAngle=2.35619 EndAngle=5.49779
    g141: ArcOfCircle CenterX=92.5869 CenterY=64.3137 CenterZ=0 NormalX=0 NormalY=0 NormalZ=1 AngleXU=0 Radius=1 StartAngle=5.49779 EndAngle=8.63938
    g142: LineSegment StartX=87.7993 StartY=60.9403 StartZ=0 EndX=91.8798 EndY=65.0208 EndZ=0
    g143: LineSegment StartX=89.2135 StartY=59.5261 StartZ=0 EndX=93.294 EndY=63.6066 EndZ=0
    g144: ArcOfCircle CenterX=96.0904 CenterY=62.8675 CenterZ=0 NormalX=0 NormalY=0 NormalZ=1 AngleXU=0 Radius=1 StartAngle=2.35619 EndAngle=5.49779
    g145: ArcOfCircle CenterX=101.56 CenterY=68.3367 CenterZ=0 NormalX=0 NormalY=0 NormalZ=1 AngleXU=0 Radius=1 StartAngle=5.49779 EndAngle=8.63938
    g146: LineSegment StartX=95.3833 StartY=63.5746 StartZ=0 EndX=100.853 EndY=69.0438 EndZ=0
    g147: LineSegment StartX=96.7975 StartY=62.1603 StartZ=0 EndX=102.267 EndY=67.6296 EndZ=0
    g148: ArcOfCircle CenterX=106.471 CenterY=68.2983 CenterZ=0 NormalX=0 NormalY=0 NormalZ=1 AngleXU=0 Radius=1 StartAngle=2.35619 EndAngle=5.49779
    g149: ArcOfCircle CenterX=110.09 CenterY=71.9177 CenterZ=0 NormalX=0 NormalY=0 NormalZ=1 AngleXU=0 Radius=1 StartAngle=5.49779 EndAngle=8.63938
    g150: LineSegment StartX=105.764 StartY=69.0054 StartZ=0 EndX=109.383 EndY=72.6248 EndZ=0
    g151: LineSegment StartX=107.178 StartY=67.5912 StartZ=0 EndX=110.797 EndY=71.2106 EndZ=0
    g152: ArcOfCircle CenterX=109.744 CenterY=66.6211 CenterZ=0 NormalX=0 NormalY=0 NormalZ=1 AngleXU=0 Radius=1 StartAngle=2.35619 EndAngle=5.49779
    g153: ArcOfCircle CenterX=111.902 CenterY=68.7797 CenterZ=0 NormalX=0 NormalY=0 NormalZ=1 AngleXU=0 Radius=1 StartAngle=5.49779 EndAngle=8.63938
    g154: LineSegment StartX=109.036 StartY=67.3282 StartZ=0 EndX=111.195 EndY=69.4868 EndZ=0
    g155: LineSegment StartX=110.451 StartY=65.914 StartZ=0 EndX=112.609 EndY=68.0726 EndZ=0
    g156: ArcOfCircle CenterX=111.856 CenterY=63.7836 CenterZ=0 NormalX=0 NormalY=0 NormalZ=1 AngleXU=0 Radius=1 StartAngle=2.35619 EndAngle=5.49779
    g157: ArcOfCircle CenterX=113.714 CenterY=65.6416 CenterZ=0 NormalX=0 NormalY=0 NormalZ=1 AngleXU=0 Radius=1 StartAngle=5.49779 EndAngle=8.63938
    g158: LineSegment StartX=111.149 StartY=64.4907 StartZ=0 EndX=113.007 EndY=66.3488 EndZ=0
    g159: LineSegment StartX=112.563 StartY=63.0765 StartZ=0 EndX=114.421 EndY=64.9345 EndZ=0
    g160: ArcOfCircle CenterX=114.206 CenterY=61.1845 CenterZ=0 NormalX=0 NormalY=0 NormalZ=1 AngleXU=0 Radius=1 StartAngle=2.35619 EndAngle=5.49779
    g161: ArcOfCircle CenterX=115.526 CenterY=62.5036 CenterZ=0 NormalX=0 NormalY=0 NormalZ=1 AngleXU=0 Radius=1 StartAngle=5.49779 EndAngle=8.63938
    g162: LineSegment StartX=113.499 StartY=61.8916 StartZ=0 EndX=114.818 EndY=63.2107 EndZ=0
    g163: LineSegment StartX=114.914 StartY=60.4774 StartZ=0 EndX=116.233 EndY=61.7965 EndZ=0
    g164: ArcOfCircle CenterX=115.61 CenterY=57.6386 CenterZ=0 NormalX=0 NormalY=0 NormalZ=1 AngleXU=0 Radius=1 StartAngle=2.35619 EndAngle=5.49779
    g165: ArcOfCircle CenterX=117.337 CenterY=59.3656 CenterZ=0 NormalX=0 NormalY=0 NormalZ=1 AngleXU=0 Radius=1 StartAngle=5.49779 EndAngle=8.63938
    g166: LineSegment StartX=114.903 StartY=58.3457 StartZ=0 EndX=116.63 EndY=60.0727 EndZ=0
    g167: LineSegment StartX=116.317 StartY=56.9315 StartZ=0 EndX=118.044 EndY=58.6585 EndZ=0
    g168: ArcOfCircle CenterX=118.119 CenterY=55.1978 CenterZ=0 NormalX=0 NormalY=0 NormalZ=1 AngleXU=0 Radius=1 StartAngle=2.35619 EndAngle=5.49779
    g169: ArcOfCircle CenterX=119.149 CenterY=56.2276 CenterZ=0 NormalX=0 NormalY=0 NormalZ=1 AngleXU=0 Radius=1 StartAngle=5.49779 EndAngle=8.63938
    g170: LineSegment StartX=117.412 StartY=55.9049 StartZ=0 EndX=118.442 EndY=56.9347 EndZ=0
    g171: LineSegment StartX=118.826 StartY=54.4907 StartZ=0 EndX=119.856 EndY=55.5205 EndZ=0
  constraints (428):
    c: Tangent(g0,g2) = 1.5708
    c: Tangent(g0,g3) = -1.5708
    c: Tangent(g1,g2) = 1.5708
    c: Tangent(g1,g3) = -1.5708
    c: Equal(g0,g1)
    c: Angle(g-1,g2) = 0.785398
    c: Radius(g0) = 1
    c: Distance(g0,g-3) = 1.5
    c: Tangent(g4,g6) = 1.5708
    c: Tangent(g4,g7) = -1.5708
    c: Tangent(g5,g6) = 1.5708
    c: Tangent(g5,g7) = -1.5708
    c: Equal(g4,g5)
    c: Angle(g-1,g6) = 0.785398
    c: Radius(g4) = 1
    c: Distance(g3,g6) = 1.5
    c: Distance(g-5,g4) = 1.5
    c: Distance(g4,g-4) = 1.5
    c: Distance(g1,g-6) = 1.5
    c: Distance(g5,g-6) = 1.5
    c: Tangent(g8,g10) = 1.5708
    c: Tangent(g8,g11) = -1.5708
    c: Tangent(g9,g10) = 1.5708
    c: Tangent(g9,g11) = -1.5708
    c: Equal(g8,g9)
    c: Angle(g-1,g10) = 0.785398
    c: Radius(g8) = 1
    c: Tangent(g12,g14) = 1.5708
    c: Tangent(g12,g15) = -1.5708
    c: Tangent(g13,g14) = 1.5708
    c: Tangent(g13,g15) = -1.5708
    c: Equal(g12,g13)
    c: Angle(g-1,g14) = 0.785398
    c: Radius(g12) = 1
    c: Tangent(g16,g18) = 1.5708
    c: Tangent(g16,g19) = -1.5708
    c: Tangent(g17,g18) = 1.5708
    c: Tangent(g17,g19) = -1.5708
    c: Equal(g16,g17)
    c: Angle(g-1,g18) = 0.785398
    c: Radius(g16) = 1
    c: Tangent(g20,g22) = 1.5708
    c: Tangent(g20,g23) = -1.5708
    c: Tangent(g21,g22) = 1.5708
    c: Tangent(g21,g23) = -1.5708
    c: Equal(g20,g21)
    c: Angle(g-1,g22) = 0.785398
    c: Radius(g20) = 1
    c: Tangent(g24,g26) = 1.5708
    c: Tangent(g24,g27) = -1.5708
    c: Tangent(g25,g26) = 1.5708
    c: Tangent(g25,g27) = -1.5708
    c: Equal(g24,g25)
    c: Angle(g-1,g26) = 0.785398
    c: Radius(g24) = 1
    c: Distance(g10,g7) = 1.5
    c: Distance(g14,g11) = 1.5
    c: Distance(g18,g15) = 1
    c: Distance(g22,g19) = 1.5
    c: Distance(g26,g23) = 1.5
    c: Distance(g8,g-5) = 1.5
    c: Distance(g9,g-6) = 1.5
    c: Distance(g13,g-6) = 1.5
    c: Distance(g17,g-6) = 1.5
    c: Distance(g12,g-10) = 1.5
    c: Distance(g16,g-7) = 1.5
    c: Distance(g20,g-8) = 1.5
    c: Distance(g21,g-6) = 1.5
    c: Distance(g25,g-6) = 1.5
    c: Distance(g24,g-8) = 1.5
    c: Tangent(g28,g30) = 1.5708
    c: Tangent(g28,g31) = -1.5708
    c: Tangent(g29,g30) = 1.5708
    c: Tangent(g29,g31) = -1.5708
    c: Equal(g28,g29)
    c: Angle(g-1,g30) = 0.785398
    c: Radius(g28) = 1
    c: Distance(g27,g30) = 1.5
    c: Distance(g28,g-9) = 1.5
    c: Distance(g29,g-6) = 1.5
    c: Tangent(g32,g34) = 1.5708
    c: Tangent(g32,g35) = -1.5708
    c: Tangent(g33,g34) = 1.5708
    c: Tangent(g33,g35) = -1.5708
    c: Equal(g32,g33)
    c: Angle(g-1,g34) = 0.785398
    c: Radius(g32) = 1
    c: Distance(g34,g31) = 1.5
    c: Distance(g32,g-13) = 1.5
    c: Distance(g-14,g33) = 1.5
    c: Tangent(g36,g38) = 1.5708
    c: Tangent(g36,g39) = -1.5708
    c: Tangent(g37,g38) = 1.5708
    c: Tangent(g37,g39) = -1.5708
    c: Equal(g36,g37)
    c: Angle(g-1,g38) = 0.785398
    c: Radius(g36) = 1
    c: Distance(g34,g39) = 1.5
    c: Distance(g36,g-15) = 1.5
    c: Distance(g37,g-11) = 1.5
    c: Tangent(g40,g42) = 1.5708
    c: Tangent(g40,g43) = -1.5708
    c: Tangent(g41,g42) = 1.5708
    c: Tangent(g41,g43) = -1.5708
    c: Equal(g40,g41)
    c: Radius(g40) = 1
    c: Tangent(g43,g39)
    c: Distance(g41,g-18) = 1.5
    c: Distance(g40,g-17) = 1.5
    c: Tangent(g44,g46) = 1.5708
    c: Tangent(g44,g47) = -1.5708
    c: Tangent(g45,g46) = 1.5708
    c: Tangent(g45,g47) = -1.5708
    c: Equal(g44,g45)
    c: Angle(g-1,g46) = 0.785398
    c: Radius(g44) = 1
    c: Tangent(g48,g50) = 1.5708
    c: Tangent(g48,g51) = -1.5708
    c: Tangent(g49,g50) = 1.5708
    c: Tangent(g49,g51) = -1.5708
    c: Equal(g48,g49)
    c: Angle(g-1,g50) = 0.785398
    c: Radius(g48) = 1
    c: Tangent(g52,g54) = 1.5708
    c: Tangent(g52,g55) = -1.5708
    c: Tangent(g53,g54) = 1.5708
    c: Tangent(g53,g55) = -1.5708
    c: Equal(g52,g53)
    c: Angle(g-1,g54) = 0.785398
    c: Radius(g52) = 1
    c: Distance(g35,g46) = 1.5
    c: Distance(g50,g47) = 1.5
    c: Distance(g54,g51) = 1.5
    c: Distance(g44,g-24) = 1.5
    c: Distance(g45,g-19) = 1.5
    c: Distance(g48,g-21) = 1.5
    c: Distance(g49,g-19) = 1.5
    c: Distance(g52,g-21) = 1.5
    c: Distance(g53,g-20) = 1.5
    c: Tangent(g56,g58) = 1.5708
    c: Tangent(g56,g59) = -1.5708
    c: Tangent(g57,g58) = 1.5708
    c: Tangent(g57,g59) = -1.5708
    c: Equal(g56,g57)
    c: Angle(g-1,g58) = 0.785398
    c: Radius(g56) = 1
    c: Tangent(g60,g62) = 1.5708
    c: Tangent(g60,g63) = -1.5708
    c: Tangent(g61,g62) = 1.5708
    c: Tangent(g61,g63) = -1.5708
    c: Equal(g60,g61)
    c: Angle(g-1,g62) = 0.785398
    c: Radius(g60) = 1
    c: Distance(g55,g58) = 1.5
    c: Distance(g62,g59) = 1.5
    c: Tangent(g64,g66) = 1.5708
    c: Tangent(g64,g67) = -1.5708
    c: Tangent(g65,g66) = 1.5708
    c: Tangent(g65,g67) = -1.5708
    c: Equal(g64,g65)
    c: Angle(g-1,g66) = 0.785398
    c: Radius(g64) = 1
    c: Tangent(g68,g70) = 1.5708
    c: Tangent(g68,g71) = -1.5708
    c: Tangent(g69,g70) = 1.5708
    c: Tangent(g69,g71) = -1.5708
    c: Equal(g68,g69)
    c: Angle(g-1,g70) = 0.785398
    c: Radius(g68) = 1
    c: Distance(g57,g-20) = 1.5
    c: Distance(g56,g-22) = 1.5
    c: Distance(g60,g-25) = 1.5
    c: Distance(g61,g-27) = 0.1
    c: Distance(g63,g66) = 1.5
    c: Distance(g70,g67) = 1.5
    c: Distance(g64,g-29) = 1.5
    c: Distance(g65,g-30) = 1.5
    c: Distance(g68,g-26) = 1.5
    c: Distance(g69,g-28) = 1.5
    c: Tangent(g72,g74) = 1.5708
    c: Tangent(g72,g75) = -1.5708
    c: Tangent(g73,g74) = 1.5708
    c: Tangent(g73,g75) = -1.5708
    c: Equal(g72,g73)
    c: Angle(g-1,g74) = 0.785398
    c: Radius(g72) = 1
    c: Tangent(g76,g78) = 1.5708
    c: Tangent(g76,g79) = -1.5708
    c: Tangent(g77,g78) = 1.5708
    c: Tangent(g77,g79) = -1.5708
    c: Equal(g76,g77)
    c: Angle(g-1,g78) = 0.785398
    c: Radius(g76) = 1
    c: Tangent(g80,g82) = 1.5708
    c: Tangent(g80,g83) = -1.5708
    c: Tangent(g81,g82) = 1.5708
    c: Tangent(g81,g83) = -1.5708
    c: Equal(g80,g81)
    c: Angle(g-1,g82) = 0.785398
    c: Radius(g80) = 1
    c: Tangent(g84,g86) = 1.5708
    c: Tangent(g84,g87) = -1.5708
    c: Tangent(g85,g86) = 1.5708
    c: Tangent(g85,g87) = -1.5708
    c: Equal(g84,g85)
    c: Angle(g-1,g86) = 0.785398
    c: Radius(g84) = 1
    c: Distance(g71,g74) = 1.5
    c: Distance(g78,g75) = 1.5
    c: Distance(g73,g-28) = 1.5
    c: Distance(g82,g79) = 1.5
    c: Distance(g86,g83) = 1.5
    c: Distance(g72,g-31) = 1.5
    c: Distance(g76,g-32) = 1.5
    c: Distance(g77,g-35) = 1.5
    c: Distance(g80,g-33) = 1.5
    c: Distance(g81,g-37) = 1.5
    c: Distance(g85,g-38) = 1.5
    c: Distance(g84,g-34) = 1.5
    c: Tangent(g88,g90) = 1.5708
    c: Tangent(g88,g91) = -1.5708
    c: Tangent(g89,g90) = 1.5708
    c: Tangent(g89,g91) = -1.5708
    c: Equal(g88,g89)
    c: Angle(g-1,g90) = 0.785398
    c: Radius(g88) = 1
    c: Tangent(g92,g94) = 1.5708
    c: Tangent(g92,g95) = -1.5708
    c: Tangent(g93,g94) = 1.5708
    c: Tangent(g93,g95) = -1.5708
    c: Equal(g92,g93)
    c: Angle(g-1,g94) = 0.785398
    c: Radius(g92) = 1
    c: Distance(g87,g90) = 1.5
    c: Distance(g94,g91) = 1.5
    c: Distance(g88,g-41) = 1.5
    c: Distance(g92,g-40) = 1.5
    c: Distance(g89,g-38) = 1.5
    c: Distance(g93,g-42) = 0.1
    c: Tangent(g96,g98) = 1.5708
    c: Tangent(g96,g99) = -1.5708
    c: Tangent(g97,g98) = 1.5708
    c: Tangent(g97,g99) = -1.5708
    c: Equal(g96,g97)
    c: Angle(g-1,g98) = 0.785398
    c: Radius(g96) = 1
    c: Tangent(g100,g102) = 1.5708
    c: Tangent(g100,g103) = -1.5708
    c: Tangent(g101,g102) = 1.5708
    c: Tangent(g101,g103) = -1.5708
    c: Equal(g100,g101)
    c: Angle(g-1,g102) = 0.785398
    c: Radius(g100) = 1
    c: Distance(g95,g98) = 1.5
    c: Distance(g102,g99) = 1.5
    c: Distance(g96,g-40) = 1.5
    c: Distance(g97,g-42) = 0.1
    c: Distance(g101,g-44) = 1.5
    c: Distance(g100,g-43) = 1.5
    c: Tangent(g104,g106) = 1.5708
    c: Tangent(g104,g107) = -1.5708
    c: Tangent(g105,g106) = 1.5708
    c: Tangent(g105,g107) = -1.5708
    c: Equal(g104,g105)
    c: Radius(g104) = 1
    c: Tangent(g107,g91)
    c: Distance(g104,g-47) = 1.5
    c: Distance(g105,g-46) = 1.5
    c: Tangent(g108,g110) = 1.5708
    c: Tangent(g108,g111) = -1.5708
    c: Tangent(g109,g110) = 1.5708
    c: Tangent(g109,g111) = -1.5708
    c: Equal(g108,g109)
    c: Angle(g-1,g110) = 0.785398
    c: Radius(g108) = 1
    c: Tangent(g112,g114) = 1.5708
    c: Tangent(g112,g115) = -1.5708
    c: Tangent(g113,g114) = 1.5708
    c: Tangent(g113,g115) = -1.5708
    c: Equal(g112,g113)
    c: Angle(g-1,g114) = 0.785398
    c: Radius(g112) = 1
    c: Tangent(g116,g118) = 1.5708
    c: Tangent(g116,g119) = -1.5708
    c: Tangent(g117,g118) = 1.5708
    c: Tangent(g117,g119) = -1.5708
    c: Equal(g116,g117)
    c: Angle(g-1,g118) = 0.785398
    c: Radius(g116) = 1
    c: Tangent(g120,g122) = 1.5708
    c: Tangent(g120,g123) = -1.5708
    c: Tangent(g121,g122) = 1.5708
    c: Tangent(g121,g123) = -1.5708
    c: Equal(g120,g121)
    c: Angle(g-1,g122) = 0.785398
    c: Radius(g120) = 1
    c: Distance(g43,g110) = 1.5
    c: Distance(g114,g111) = 1.5
    c: Distance(g118,g115) = 1.5
    c: Distance(g122,g119) = 1.5
    c: Distance(g109,g-18) = 1.5
    c: Distance(g113,g-18) = 1.5
    c: Distance(g-48,g108) = 1.5
    c: Distance(g112,g-48) = 1.5
    c: Distance(g116,g-49) = 1.5
    c: Distance(g117,g-18) = 1.5
    c: Distance(g-50,g120) = 1.5
    c: Distance(g121,g-18) = 1.5
    c: Tangent(g124,g126) = 1.5708
    c: Tangent(g124,g127) = -1.5708
    c: Tangent(g125,g126) = 1.5708
    c: Tangent(g125,g127) = -1.5708
    c: Equal(g124,g125)
    c: Angle(g-1,g126) = 0.785398
    c: Radius(g124) = 1
    c: Tangent(g128,g130) = 1.5708
    c: Tangent(g128,g131) = -1.5708
    c: Tangent(g129,g130) = 1.5708
    c: Tangent(g129,g131) = -1.5708
    c: Equal(g128,g129)
    c: Angle(g-1,g130) = 0.785398
    c: Radius(g128) = 1
    c: Tangent(g132,g134) = 1.5708
    c: Tangent(g132,g135) = -1.5708
    c: Tangent(g133,g134) = 1.5708
    c: Tangent(g133,g135) = -1.5708
    c: Equal(g132,g133)
    c: Angle(g-1,g134) = 0.785398
    c: Radius(g132) = 1
    c: Tangent(g136,g138) = 1.5708
    c: Tangent(g136,g139) = -1.5708
    c: Tangent(g137,g138) = 1.5708
    c: Tangent(g137,g139) = -1.5708
    c: Equal(g136,g137)
    c: Angle(g-1,g138) = 0.785398
    c: Radius(g136) = 1
    c: Distance(g123,g126) = 1.5
    c: Distance(g130,g127) = 1.5
    c: Distance(g125,g-52) = 1.5
    c: Distance(g-51,g124) = 1.5
    c: Distance(g-51,g128) = 1.5
    c: Distance(g131,g134) = 1.5
    c: Distance(g138,g135) = 1.5
    c: Distance(g133,g-52) = 1.5
    c: Distance(g129,g-52) = 1.5
    c: Distance(g-56,g132) = 1.5
    c: Distance(g-52,g137) = 1.5
    c: Distance(g136,g-57) = 1.5
    c: Tangent(g140,g142) = 1.5708
    c: Tangent(g140,g143) = -1.5708
    c: Tangent(g141,g142) = 1.5708
    c: Tangent(g141,g143) = -1.5708
    c: Equal(g140,g141)
    c: Angle(g-1,g142) = 0.785398
    c: Radius(g140) = 1
    c: Tangent(g144,g146) = 1.5708
    c: Tangent(g144,g147) = -1.5708
    c: Tangent(g145,g146) = 1.5708
    c: Tangent(g145,g147) = -1.5708
    c: Equal(g144,g145)
    c: Angle(g-1,g146) = 0.785398
    c: Radius(g144) = 1
    c: Distance(g139,g142) = 1.5
    c: Distance(g146,g143) = 1.5
    c: Distance(g140,g-55) = 1.5
    c: Distance(g141,g-52) = 1.5
    c: Distance(g145,g-52) = 1.5
    c: Distance(g144,g-58) = 1.5
    c: Tangent(g148,g150) = 1.5708
    c: Tangent(g148,g151) = -1.5708
    c: Tangent(g149,g150) = 1.5708
    c: Tangent(g149,g151) = -1.5708
    c: Equal(g148,g149)
    c: Angle(g-1,g150) = 0.785398
    c: Radius(g148) = 1
    c: Distance(g147,g150) = 1.5
    c: Distance(g149,g-59) = 1.5
    c: Distance(g148,g-60) = 1.5
    c: Tangent(g152,g154) = 1.5708
    c: Tangent(g152,g155) = -1.5708
    c: Tangent(g153,g154) = 1.5708
    c: Tangent(g153,g155) = -1.5708
    c: Equal(g152,g153)
    c: Angle(g-1,g154) = 0.785398
    c: Radius(g152) = 1
    c: Distance(g151,g154) = 1.5
    c: Distance(g152,g-61) = 1.5
    c: Distance(g153,g-59) = 1.5
    c: Tangent(g156,g158) = 1.5708
    c: Tangent(g156,g159) = -1.5708
    c: Tangent(g157,g158) = 1.5708
    c: Tangent(g157,g159) = -1.5708
    c: Equal(g156,g157)
    c: Angle(g-1,g158) = 0.785398
    c: Radius(g156) = 1
    c: Tangent(g160,g162) = 1.5708
    c: Tangent(g160,g163) = -1.5708
    c: Tangent(g161,g162) = 1.5708
    c: Tangent(g161,g163) = -1.5708
    c: Equal(g160,g161)
    c: Angle(g-1,g162) = 0.785398
    c: Radius(g160) = 1
    c: Tangent(g164,g166) = 1.5708
    c: Tangent(g164,g167) = -1.5708
    c: Tangent(g165,g166) = 1.5708
    c: Tangent(g165,g167) = -1.5708
    c: Equal(g164,g165)
    c: Angle(g-1,g166) = 0.785398
    c: Radius(g164) = 1
    c: Tangent(g168,g170) = 1.5708
    c: Tangent(g168,g171) = -1.5708
    c: Tangent(g169,g170) = 1.5708
    c: Tangent(g169,g171) = -1.5708
    c: Equal(g168,g169)
    c: Angle(g-1,g170) = 0.785398
    c: Radius(g168) = 1
    c: Distance(g155,g158) = 1.5
    c: Distance(g159,g162) = 1.5
    c: Distance(g166,g163) = 1.5
    c: Distance(g170,g167) = 1.5
    c: Distance(g156,g-62) = 1.5
    c: Distance(g161,g-59) = 1.5
    c: Distance(g160,g-62) = 1.5
    c: Distance(g157,g-59) = 1.5
    c: Distance(g165,g-59) = 1.5
    c: Distance(g169,g-59) = 1.5
    c: Distance(g164,g-64) = 1.5
    c: Distance(g168,g-65) = 1.5
FEATURE [PartDesign::Pocket] Pocket002
  BaseFeature = -> LinearPattern001
  Direction = (0,0,1)
  Length = 5
  Length2 = 5
  Profile = -> Sketch006
  ReferenceAxis = -> Sketch006 [N_Axis]
  Suppressed = false
  Type = 1
FEATURE [Sketcher::SketchObject] Sketch007
  AttachmentSupport = -> [Pocket002]
  ExternalGeometry = -> [Pocket002]
  FullyConstrained = true
  MapMode = 5
  Placement = pos=(0,0,0) rot=(1,0,0;3.14159rad)
  sketch-geometry (89):
    g0: ArcOfCircle CenterX=107.2 CenterY=-3.8 CenterZ=0 NormalX=0 NormalY=0 NormalZ=1 AngleXU=0 Radius=1.25 StartAngle=3.14159 EndAngle=6.28319
    g1: ArcOfCircle CenterX=107.2 CenterY=24.1 CenterZ=0 NormalX=0 NormalY=0 NormalZ=1 AngleXU=0 Radius=1.25 StartAngle=9e-16 EndAngle=3.14159
    g2: LineSegment StartX=105.95 StartY=-3.8 StartZ=0 EndX=105.95 EndY=24.1 EndZ=0
    g3: LineSegment StartX=108.45 StartY=-3.8 StartZ=0 EndX=108.45 EndY=24.1 EndZ=0
    g4: ArcOfCircle CenterX=122.44 CenterY=-3.8 CenterZ=0 NormalX=0 NormalY=0 NormalZ=1 AngleXU=0 Radius=1.25 StartAngle=3.14159 EndAngle=6.28319
    g5: ArcOfCircle CenterX=122.44 CenterY=24.1 CenterZ=0 NormalX=0 NormalY=0 NormalZ=1 AngleXU=0 Radius=1.25 StartAngle=0 EndAngle=3.14159
    g6: LineSegment StartX=121.19 StartY=-3.8 StartZ=0 EndX=121.19 EndY=24.1 EndZ=0
    g7: LineSegment StartX=123.69 StartY=-3.8 StartZ=0 EndX=123.69 EndY=24.1 EndZ=0
    g8: LineSegment StartX=125.2 StartY=43.4 StartZ=0 EndX=125.2 EndY=39.4 EndZ=0
    g9: LineSegment StartX=125.2 StartY=39.4 StartZ=0 EndX=122.7 EndY=39.4 EndZ=0
    g10: LineSegment StartX=122.7 StartY=39.4 StartZ=0 EndX=122.7 EndY=43.4 EndZ=0
    g11: LineSegment StartX=122.7 StartY=43.4 StartZ=0 EndX=125.2 EndY=43.4 EndZ=0
    g12: ArcOfCircle CenterX=107.2 CenterY=32.9 CenterZ=0 NormalX=0 NormalY=0 NormalZ=1 AngleXU=0 Radius=1.25 StartAngle=3.14159 EndAngle=6.28319
    g13: ArcOfCircle CenterX=107.2 CenterY=37.9 CenterZ=0 NormalX=0 NormalY=0 NormalZ=1 AngleXU=0 Radius=1.25 StartAngle=1.5e-15 EndAngle=3.14159
    g14: LineSegment StartX=105.95 StartY=32.9 StartZ=0 EndX=105.95 EndY=37.9 EndZ=0
    g15: LineSegment StartX=108.45 StartY=32.9 StartZ=0 EndX=108.45 EndY=37.9 EndZ=0
    g16: ArcOfCircle CenterX=121.7 CenterY=37.9 CenterZ=0 NormalX=0 NormalY=0 NormalZ=1 AngleXU=0 Radius=1.25 StartAngle=0 EndAngle=2.85184
    g17: ArcOfCircle CenterX=121.7 CenterY=32.9 CenterZ=0 NormalX=0 NormalY=0 NormalZ=1 AngleXU=0 Radius=1.25 StartAngle=3.43134 EndAngle=6.28319
    g18: LineSegment StartX=122.95 StartY=37.9 StartZ=0 EndX=122.95 EndY=32.9 EndZ=0
    g19: ArcOfCircle CenterX=109.039 CenterY=41.168 CenterZ=0 NormalX=0 NormalY=0 NormalZ=1 AngleXU=0 Radius=1 StartAngle=2.35619 EndAngle=5.49779
    g20: ArcOfCircle CenterX=120.961 CenterY=53.0896 CenterZ=0 NormalX=0 NormalY=0 NormalZ=1 AngleXU=0 Radius=1 StartAngle=5.49779 EndAngle=8.63938
    g21: LineSegment StartX=108.332 StartY=41.8751 StartZ=0 EndX=120.254 EndY=53.7967 EndZ=0
    g22: LineSegment StartX=109.746 StartY=40.4609 StartZ=0 EndX=121.668 EndY=52.3825 EndZ=0
    g23: ArcOfCircle CenterX=110.95 CenterY=38.1291 CenterZ=0 NormalX=0 NormalY=0 NormalZ=1 AngleXU=0 Radius=1 StartAngle=2.35619 EndAngle=5.49779
    g24: ArcOfCircle CenterX=122.8 CenterY=49.9791 CenterZ=0 NormalX=0 NormalY=0 NormalZ=1 AngleXU=0 Radius=1 StartAngle=5.49779 EndAngle=8.63938
    g25: LineSegment StartX=110.243 StartY=38.8362 StartZ=0 EndX=122.093 EndY=50.6862 EndZ=0
    g26: LineSegment StartX=111.657 StartY=37.422 StartZ=0 EndX=123.507 EndY=49.272 EndZ=0
    g27: LineSegment StartX=120.023 StartY=32.9 StartZ=0 EndX=118.2 EndY=32.9 EndZ=0
    g28: LineSegment StartX=117.7 StartY=33.4 StartZ=0 EndX=117.7 EndY=37.4 EndZ=0
    g29: LineSegment StartX=118.2 StartY=37.9 StartZ=0 EndX=120.023 EndY=37.9 EndZ=0
    g30: ArcOfCircle CenterX=118.2 CenterY=37.4 CenterZ=0 NormalX=0 NormalY=0 NormalZ=1 AngleXU=0 Radius=0.5 StartAngle=1.5708 EndAngle=3.14159
    g31: GeomPoint X=117.7 Y=37.9 Z=0
    g32: ArcOfCircle CenterX=118.2 CenterY=33.4 CenterZ=0 NormalX=0 NormalY=0 NormalZ=1 AngleXU=0 Radius=0.5 StartAngle=3.14159 EndAngle=4.71239
    g33: ArcOfCircle CenterX=120.023 CenterY=32.4 CenterZ=0 NormalX=0 NormalY=0 NormalZ=1 AngleXU=0 Radius=0.5 StartAngle=0.289752 EndAngle=1.5708
    g34: ArcOfCircle CenterX=120.023 CenterY=38.4 CenterZ=0 NormalX=0 NormalY=0 NormalZ=1 AngleXU=0 Radius=0.5 StartAngle=4.71239 EndAngle=5.99343
    g35: GeomPoint X=117.7 Y=35.4 Z=0
    g36: GeomPoint X=122.95 Y=35.4 Z=0
    g37: ArcOfCircle CenterX=118.171 CenterY=40.4 CenterZ=0 NormalX=0 NormalY=0 NormalZ=1 AngleXU=0 Radius=1 StartAngle=2.35619 EndAngle=5.49779
    g38: ArcOfCircle CenterX=122.8 CenterY=45.0293 CenterZ=0 NormalX=0 NormalY=0 NormalZ=1 AngleXU=0 Radius=1 StartAngle=5.49779 EndAngle=8.63938
    g39: LineSegment StartX=117.464 StartY=41.1071 StartZ=0 EndX=122.093 EndY=45.7364 EndZ=0
    g40: LineSegment StartX=118.878 StartY=39.6929 StartZ=0 EndX=123.507 EndY=44.3222 EndZ=0
    g41: ArcOfCircle CenterX=110.94 CenterY=33.1696 CenterZ=0 NormalX=0 NormalY=0 NormalZ=1 AngleXU=0 Radius=1 StartAngle=2.35619 EndAngle=5.49779
    g42: ArcOfCircle CenterX=115.2 CenterY=37.4293 CenterZ=0 NormalX=0 NormalY=0 NormalZ=1 AngleXU=0 Radius=1 StartAngle=5.49779 EndAngle=8.63938
    g43: LineSegment StartX=110.233 StartY=33.8767 StartZ=0 EndX=114.493 EndY=38.1365 EndZ=0
    g44: LineSegment StartX=111.647 StartY=32.4625 StartZ=0 EndX=115.907 EndY=36.7222 EndZ=0
    g45: ArcOfCircle CenterX=109.655 CenterY=26.9346 CenterZ=0 NormalX=0 NormalY=0 NormalZ=1 AngleXU=0 Radius=1 StartAngle=2.35619 EndAngle=5.49779
    g46: ArcOfCircle CenterX=115.311 CenterY=32.5908 CenterZ=0 NormalX=0 NormalY=0 NormalZ=1 AngleXU=0 Radius=1 StartAngle=5.49779 EndAngle=8.63938
    g47: LineSegment StartX=108.948 StartY=27.6418 StartZ=0 EndX=114.604 EndY=33.2979 EndZ=0
    g48: LineSegment StartX=110.362 StartY=26.2275 StartZ=0 EndX=116.018 EndY=31.8837 EndZ=0
    g49: ArcOfCircle CenterX=110.95 CenterY=23.2799 CenterZ=0 NormalX=0 NormalY=0 NormalZ=1 AngleXU=0 Radius=1 StartAngle=2.35619 EndAngle=5.49779
    g50: ArcOfCircle CenterX=118.07 CenterY=30.4 CenterZ=0 NormalX=0 NormalY=0 NormalZ=1 AngleXU=0 Radius=1 StartAngle=5.49779 EndAngle=8.63938
    g51: LineSegment StartX=110.243 StartY=23.987 StartZ=0 EndX=117.363 EndY=31.1071 EndZ=0
    g52: LineSegment StartX=111.657 StartY=22.5727 StartZ=0 EndX=118.777 EndY=29.6929 EndZ=0
    g53: ArcOfCircle CenterX=110.95 CenterY=18.3301 CenterZ=0 NormalX=0 NormalY=0 NormalZ=1 AngleXU=0 Radius=1 StartAngle=2.35619 EndAngle=5.49779
    g54: ArcOfCircle CenterX=121.771 CenterY=29.1507 CenterZ=0 NormalX=0 NormalY=0 NormalZ=1 AngleXU=0 Radius=1 StartAngle=5.49779 EndAngle=8.63938
    g55: LineSegment StartX=110.243 StartY=19.0372 StartZ=0 EndX=121.063 EndY=29.8578 EndZ=0
    g56: LineSegment StartX=111.657 StartY=17.623 StartZ=0 EndX=122.478 EndY=28.4436 EndZ=0
    g57: ArcOfCircle CenterX=110.95 CenterY=13.3804 CenterZ=0 NormalX=0 NormalY=0 NormalZ=1 AngleXU=0 Radius=1 StartAngle=2.35619 EndAngle=5.49779
    g58: ArcOfCircle CenterX=118.69 CenterY=21.1204 CenterZ=0 NormalX=0 NormalY=0 NormalZ=1 AngleXU=0 Radius=1 StartAngle=5.49779 EndAngle=8.63938
    g59: LineSegment StartX=110.243 StartY=14.0875 StartZ=0 EndX=117.983 EndY=21.8275 EndZ=0
    g60: LineSegment StartX=111.657 StartY=12.6733 StartZ=0 EndX=119.397 EndY=20.4132 EndZ=0
    g61: ArcOfCircle CenterX=110.95 CenterY=8.43061 CenterZ=0 NormalX=0 NormalY=0 NormalZ=1 AngleXU=0 Radius=1 StartAngle=2.35619 EndAngle=5.49779
    g62: ArcOfCircle CenterX=118.69 CenterY=16.1706 CenterZ=0 NormalX=0 NormalY=0 NormalZ=1 AngleXU=0 Radius=1 StartAngle=5.49779 EndAngle=8.63938
    g63: LineSegment StartX=110.243 StartY=9.13772 StartZ=0 EndX=117.983 EndY=16.8777 EndZ=0
    g64: LineSegment StartX=111.657 StartY=7.7235 StartZ=0 EndX=119.397 EndY=15.4635 EndZ=0
    g65: ArcOfCircle CenterX=110.95 CenterY=3.48086 CenterZ=0 NormalX=0 NormalY=0 NormalZ=1 AngleXU=0 Radius=1 StartAngle=2.35619 EndAngle=5.49779
    g66: ArcOfCircle CenterX=118.69 CenterY=11.2209 CenterZ=0 NormalX=0 NormalY=0 NormalZ=1 AngleXU=0 Radius=1 StartAngle=5.49779 EndAngle=8.63938
    g67: LineSegment StartX=110.243 StartY=4.18797 StartZ=0 EndX=117.983 EndY=11.928 EndZ=0
    g68: LineSegment StartX=111.657 StartY=2.77376 StartZ=0 EndX=119.397 EndY=10.5138 EndZ=0
    g69: ArcOfCircle CenterX=110.95 CenterY=-1.46888 CenterZ=0 NormalX=0 NormalY=0 NormalZ=1 AngleXU=0 Radius=1 StartAngle=2.35619 EndAngle=5.49779
    g70: ArcOfCircle CenterX=118.69 CenterY=6.27112 CenterZ=0 NormalX=0 NormalY=0 NormalZ=1 AngleXU=0 Radius=1 StartAngle=5.49779 EndAngle=8.63938
    g71: LineSegment StartX=110.243 StartY=-0.761775 StartZ=0 EndX=117.983 EndY=6.97822 EndZ=0
    g72: LineSegment StartX=111.657 StartY=-2.17599 StartZ=0 EndX=119.397 EndY=5.56401 EndZ=0
    g73: ArcOfCircle CenterX=110.469 CenterY=-6.9 CenterZ=0 NormalX=0 NormalY=0 NormalZ=1 AngleXU=0 Radius=1 StartAngle=2.35619 EndAngle=5.49779
    g74: ArcOfCircle CenterX=118.69 CenterY=1.32137 CenterZ=0 NormalX=0 NormalY=0 NormalZ=1 AngleXU=0 Radius=1 StartAngle=5.49779 EndAngle=8.63938
    g75: LineSegment StartX=109.762 StartY=-6.19289 StartZ=0 EndX=117.983 EndY=2.02848 EndZ=0
    g76: LineSegment StartX=111.176 StartY=-7.60711 StartZ=0 EndX=119.397 EndY=0.614262 EndZ=0
    g77: ArcOfCircle CenterX=115.418 CenterY=-6.9 CenterZ=0 NormalX=0 NormalY=0 NormalZ=1 AngleXU=0 Radius=1 StartAngle=2.35619 EndAngle=5.49779
    g78: ArcOfCircle CenterX=118.69 CenterY=-3.62838 CenterZ=0 NormalX=0 NormalY=0 NormalZ=1 AngleXU=0 Radius=1 StartAngle=5.49779 EndAngle=8.63938
    g79: LineSegment StartX=114.711 StartY=-6.19289 StartZ=0 EndX=117.983 EndY=-2.92127 EndZ=0
    g80: LineSegment StartX=116.125 StartY=-7.60711 StartZ=0 EndX=119.397 EndY=-4.33548 EndZ=0
    g81: ArcOfCircle CenterX=120.368 CenterY=-6.9 CenterZ=0 NormalX=0 NormalY=0 NormalZ=1 AngleXU=0 Radius=1 StartAngle=2.35619 EndAngle=5.49779
    g82: ArcOfCircle CenterX=120.425 CenterY=-6.84329 CenterZ=0 NormalX=0 NormalY=0 NormalZ=1 AngleXU=0 Radius=1 StartAngle=5.49779 EndAngle=8.63938
    g83: LineSegment StartX=119.661 StartY=-6.19289 StartZ=0 EndX=119.718 EndY=-6.13618 EndZ=0
    g84: LineSegment StartX=121.075 StartY=-7.60711 StartZ=0 EndX=121.132 EndY=-7.5504 EndZ=0
    g85: ArcOfCircle CenterX=84.1455 CenterY=21.316 CenterZ=0 NormalX=0 NormalY=0 NormalZ=1 AngleXU=0 Radius=1 StartAngle=2.35619 EndAngle=5.49779
    g86: ArcOfCircle CenterX=88.8122 CenterY=25.9826 CenterZ=0 NormalX=0 NormalY=0 NormalZ=1 AngleXU=0 Radius=1 StartAngle=5.49779 EndAngle=8.63938
    g87: LineSegment StartX=83.4384 StartY=22.0231 StartZ=0 EndX=88.1051 EndY=26.6898 EndZ=0
    g88: LineSegment StartX=84.8526 StartY=20.6089 StartZ=0 EndX=89.5193 EndY=25.2755 EndZ=0
  constraints (222):
    c: Tangent(g0,g2) = 1.5708
    c: Tangent(g0,g3) = -1.5708
    c: Tangent(g1,g2) = 1.5708
    c: Tangent(g1,g3) = -1.5708
    c: Equal(g0,g1)
    c: Vertical(g3)
    c: Radius(g0) = 1.25
    c: DistanceX(g-1,g0) = 107.2
    c: DistanceY(g0,g-1) = 3.8
    c: DistanceY(g0,g1) = 27.9
    c: Tangent(g4,g6) = 1.5708
    c: Tangent(g4,g7) = -1.5708
    c: Tangent(g5,g6) = 1.5708
    c: Tangent(g5,g7) = -1.5708
    c: Equal(g4,g5)
    c: Vertical(g7)
    c: Radius(g4) = 1.25
    c: DistanceX(g0,g4) = 15.24
    c: Horizontal(g4,g0)
    c: Horizontal(g5,g1)
    c: Coincident(g8,g9)
    c: Coincident(g9,g10)
    c: Coincident(g10,g11)
    c: Coincident(g11,g8)
    c: Vertical(g8)
    c: Vertical(g10)
    c: Horizontal(g9)
    c: Horizontal(g11)
    c: Distance(g5,g11) = 19.3
    c: Distance(g9,g9) = 2.5
    c: Distance(g-3,g8) = 0.1
    c: DistanceY(g10,g10) = 4
    c: Tangent(g12,g14) = 1.5708
    c: Tangent(g12,g15) = -1.5708
    c: Tangent(g13,g14) = 1.5708
    c: Tangent(g13,g15) = -1.5708
    c: Equal(g12,g13)
    c: Radius(g12) = 1.25
    c: Vertical(g14)
    c: Vertical(g12,g1)
    c: DistanceY(g1,g12) = 8.8
    c: DistanceY(g12,g13) = 5
    c: Tangent(g16,g18) = 1.5708
    c: Tangent(g17,g18) = 1.5708
    c: Equal(g16,g17)
    c: Radius(g16) = 1.25
    c: Horizontal(g17,g12)
    c: Horizontal(g16,g13)
    c: DistanceX(g12,g17) = 14.5
    c: Tangent(g19,g21) = 1.5708
    c: Tangent(g19,g22) = -1.5708
    c: Tangent(g20,g21) = 1.5708
    c: Tangent(g20,g22) = -1.5708
    c: Equal(g19,g20)
    c: Angle(g-1,g21) = 0.785398
    c: Radius(g19) = 1
    c: Distance(g-5,g21) = 1.5
    c: Distance(g19,g13) = 1.5
    c: Distance(g20,g-4) = 1.5
    c: Tangent(g23,g25) = 1.5708
    c: Tangent(g23,g26) = -1.5708
    c: Tangent(g24,g25) = 1.5708
    c: Tangent(g24,g26) = -1.5708
    c: Equal(g23,g24)
    c: Angle(g-1,g25) = 0.785398
    c: Radius(g23) = 1
    c: Distance(g22,g25) = 1.5
    c: Distance(g23,g15) = 1.5
    c: Distance(g24,g-3) = 1.5
    c: Horizontal(g29)
    c: Horizontal(g27)
    c: Vertical(g18)
    c: PointOnObject(g31,g28)
    c: PointOnObject(g31,g29)
    c: Tangent(g28,g30) = 1.5708
    c: Tangent(g29,g30) = 1.5708
    c: Tangent(g28,g32) = 1.5708
    c: Tangent(g27,g32) = 1.5708
    c: Equal(g32,g30)
    c: Vertical(g28)
    c: Tangent(g27,g33) = -1.5708
    c: Tangent(g17,g33) = 1.5708
    c: Tangent(g29,g34) = -1.5708
    c: Tangent(g16,g34) = 1.5708
    c: Equal(g34,g33)
    c: Equal(g33,g30)
    c: Radius(g30) = 0.5
    c: Distance(g17,g28) = 4
    c: Distance(g27,g29) = 5
    c: Symmetric(g28,g28,g35)
    c: Symmetric(g18,g18,g36)
    c: Horizontal(g35,g36)
    c: Tangent(g37,g39) = 1.5708
    c: Tangent(g37,g40) = -1.5708
    c: Tangent(g38,g39) = 1.5708
    c: Tangent(g38,g40) = -1.5708
    c: Equal(g37,g38)
    c: Angle(g-1,g39) = 0.785398
    c: Radius(g37) = 1
    c: Distance(g26,g39) = 1.5
    c: Distance(g38,g-3) = 1.5
    c: Distance(g37,g29) = 1.5
    c: Tangent(g41,g43) = 1.5708
    c: Tangent(g41,g44) = -1.5708
    c: Tangent(g42,g43) = 1.5708
    c: Tangent(g42,g44) = -1.5708
    c: Equal(g41,g42)
    c: Angle(g-1,g43) = 0.785398
    c: Radius(g41) = 1
    c: Tangent(g45,g47) = 1.5708
    c: Tangent(g45,g48) = -1.5708
    c: Tangent(g46,g47) = 1.5708
    c: Tangent(g46,g48) = -1.5708
    c: Equal(g45,g46)
    c: Angle(g-1,g47) = 0.785398
    c: Radius(g45) = 1
    c: Tangent(g49,g51) = 1.5708
    c: Tangent(g49,g52) = -1.5708
    c: Tangent(g50,g51) = 1.5708
    c: Tangent(g50,g52) = -1.5708
    c: Equal(g49,g50)
    c: Angle(g-1,g51) = 0.785398
    c: Radius(g49) = 1
    c: Tangent(g53,g55) = 1.5708
    c: Tangent(g53,g56) = -1.5708
    c: Tangent(g54,g55) = 1.5708
    c: Tangent(g54,g56) = -1.5708
    c: Equal(g53,g54)
    c: Angle(g-1,g55) = 0.785398
    c: Radius(g53) = 1
    c: Distance(g26,g43) = 1.5
    c: Distance(g44,g47) = 1.5
    c: Distance(g51,g48) = 1.5
    c: Distance(g55,g52) = 1.5
    c: Tangent(g57,g59) = 1.5708
    c: Tangent(g57,g60) = -1.5708
    c: Tangent(g58,g59) = 1.5708
    c: Tangent(g58,g60) = -1.5708
    c: Equal(g57,g58)
    c: Angle(g-1,g59) = 0.785398
    c: Radius(g57) = 1
    c: Tangent(g61,g63) = 1.5708
    c: Tangent(g61,g64) = -1.5708
    c: Tangent(g62,g63) = 1.5708
    c: Tangent(g62,g64) = -1.5708
    c: Equal(g61,g62)
    c: Angle(g-1,g63) = 0.785398
    c: Radius(g61) = 1
    c: Tangent(g65,g67) = 1.5708
    c: Tangent(g65,g68) = -1.5708
    c: Tangent(g66,g67) = 1.5708
    c: Tangent(g66,g68) = -1.5708
    c: Equal(g65,g66)
    c: Angle(g-1,g67) = 0.785398
    c: Radius(g65) = 1
    c: Distance(g59,g56) = 1.5
    c: Distance(g63,g60) = 1.5
    c: Distance(g45,g1) = 1.5
    c: Distance(g41,g12) = 1.5
    c: Distance(g42,g28) = 1.5
    c: Distance(g46,g32) = 1.5
    c: Distance(g49,g3) = 1.5
    c: Distance(g50,g27) = 1.5
    c: Distance(g54,g17) = 1.5
    c: Distance(g53,g3) = 1.5
    c: Distance(g58,g6) = 1.5
    c: Distance(g57,g3) = 1.5
    c: Distance(g62,g6) = 1.5
    c: Distance(g61,g3) = 1.5
    c: Distance(g64,g67) = 1.5
    c: Distance(g66,g6) = 1.5
    c: Distance(g65,g3) = 1.5
    c: Tangent(g69,g71) = 1.5708
    c: Tangent(g69,g72) = -1.5708
    c: Tangent(g70,g71) = 1.5708
    c: Tangent(g70,g72) = -1.5708
    c: Equal(g69,g70)
    c: Angle(g-1,g71) = 0.785398
    c: Radius(g69) = 1
    c: Distance(g68,g71) = 1.5
    c: Distance(g70,g6) = 1.5
    c: Distance(g69,g3) = 1.5
    c: Tangent(g73,g75) = 1.5708
    c: Tangent(g73,g76) = -1.5708
    c: Tangent(g74,g75) = 1.5708
    c: Tangent(g74,g76) = -1.5708
    c: Equal(g73,g74)
    c: Angle(g-1,g75) = 0.785398
    c: Radius(g73) = 1
    c: Distance(g72,g75) = 1.5
    c: Distance(g74,g6) = 1.5
    c: Distance(g73,g-6) = 1.5
    c: Tangent(g77,g79) = 1.5708
    c: Tangent(g77,g80) = -1.5708
    c: Tangent(g78,g79) = 1.5708
    c: Tangent(g78,g80) = -1.5708
    c: Equal(g77,g78)
    c: Angle(g-1,g79) = 0.785398
    c: Radius(g77) = 1
    c: Distance(g76,g79) = 1.5
    c: Distance(g78,g6) = 1.5
    c: Distance(g77,g-6) = 1.5
    c: Tangent(g81,g83) = 1.5708
    c: Tangent(g81,g84) = -1.5708
    c: Tangent(g82,g83) = 1.5708
    c: Tangent(g82,g84) = -1.5708
    c: Equal(g81,g82)
    c: Angle(g-1,g83) = 0.785398
    c: Radius(g81) = 1
    c: Distance(g80,g83) = 1.5
    c: Distance(g81,g-6) = 1.5
    c: Distance(g82,g4) = 1.4
    c: Tangent(g85,g87) = 1.5708
    c: Tangent(g85,g88) = -1.5708
    c: Tangent(g86,g87) = 1.5708
    c: Tangent(g86,g88) = -1.5708
    c: Equal(g85,g86)
    c: Angle(g-1,g87) = 0.785398
    c: Radius(g85) = 1
    c: Distance(g-7,g88) = 1.5
    c: Distance(g86,g-8) = 1.5
    c: Horizontal(g85,g-7)
FEATURE [PartDesign::Pocket] Pocket003
  BaseFeature = -> Pocket002
  Direction = (0,0,1)
  Length = 5
  Length2 = 5
  Profile = -> Sketch007
  ReferenceAxis = -> Sketch007 [N_Axis]
  Suppressed = false
  Type = 1
FEATURE [PartDesign::Pad] Pad003
  BaseFeature = -> Pocket003
  Direction = (0,0,-1)
  Length = 10
  Length2 = 10
  Profile = -> Sketch004
  ReferenceAxis = -> Sketch004 [N_Axis]
  Reversed = true
  Suppressed = false
  Type = 3
  UpToFace = -> Pocket003 [Face4]
FEATURE [Sketcher::SketchObject] Sketch008
  AttachmentSupport = -> [Pad003]
  ExternalGeometry = -> [Pad003]
  FullyConstrained = true
  MapMode = 5
  Placement = pos=(0,0,-1.6) rot=(1,0,0;3.14159rad)
  sketch-geometry (5):
    g0: Circle CenterX=9.5 CenterY=28.5 CenterZ=0 NormalX=0 NormalY=0 NormalZ=1 AngleXU=0 Radius=1.05
    g1: Circle CenterX=9.5 CenterY=9.5 CenterZ=0 NormalX=0 NormalY=0 NormalZ=1 AngleXU=0 Radius=1.05
    g2: Circle CenterX=85.5 CenterY=5.5 CenterZ=0 NormalX=0 NormalY=0 NormalZ=1 AngleXU=0 Radius=1.05
    g3: Circle CenterX=56.5 CenterY=42.9 CenterZ=0 NormalX=0 NormalY=0 NormalZ=1 AngleXU=0 Radius=1.05
    g4: Circle CenterX=101.5 CenterY=47.5 CenterZ=0 NormalX=0 NormalY=0 NormalZ=1 AngleXU=0 Radius=1.05
  constraints (10):
    c: Coincident(g0,g-4)
    c: Coincident(g1,g-3)
    c: Coincident(g2,g-7)
    c: Coincident(g3,g-5)
    c: Coincident(g4,g-6)
    c: Equal(g3,g0)
    c: Equal(g0,g1)
    c: Equal(g1,g2)
    c: Equal(g2,g4)
    c: Diameter(g0) = 2.1
FEATURE [PartDesign::Pocket] Pocket004
  BaseFeature = -> Pad003
  Direction = (0,0,1)
  Length = 5
  Length2 = 5
  Profile = -> Sketch008
  ReferenceAxis = -> Sketch008 [N_Axis]
  Suppressed = false
  Type = 1
FEATURE [PartDesign::Body] Body003
  BaseFeature = -> Cut002
  Group = -> [BaseFeature,DatumPlane,Sketch003,Pocket,LinearPattern,Sketch004,Pad002,Sketch005,Pocket001,LinearPattern001,Sketch006,Pocket002,Sketch007,Pocket003,Pad003,Sketch008,Pocket004]
  Origin = -> Origin003
  Tip = -> Pocket004
